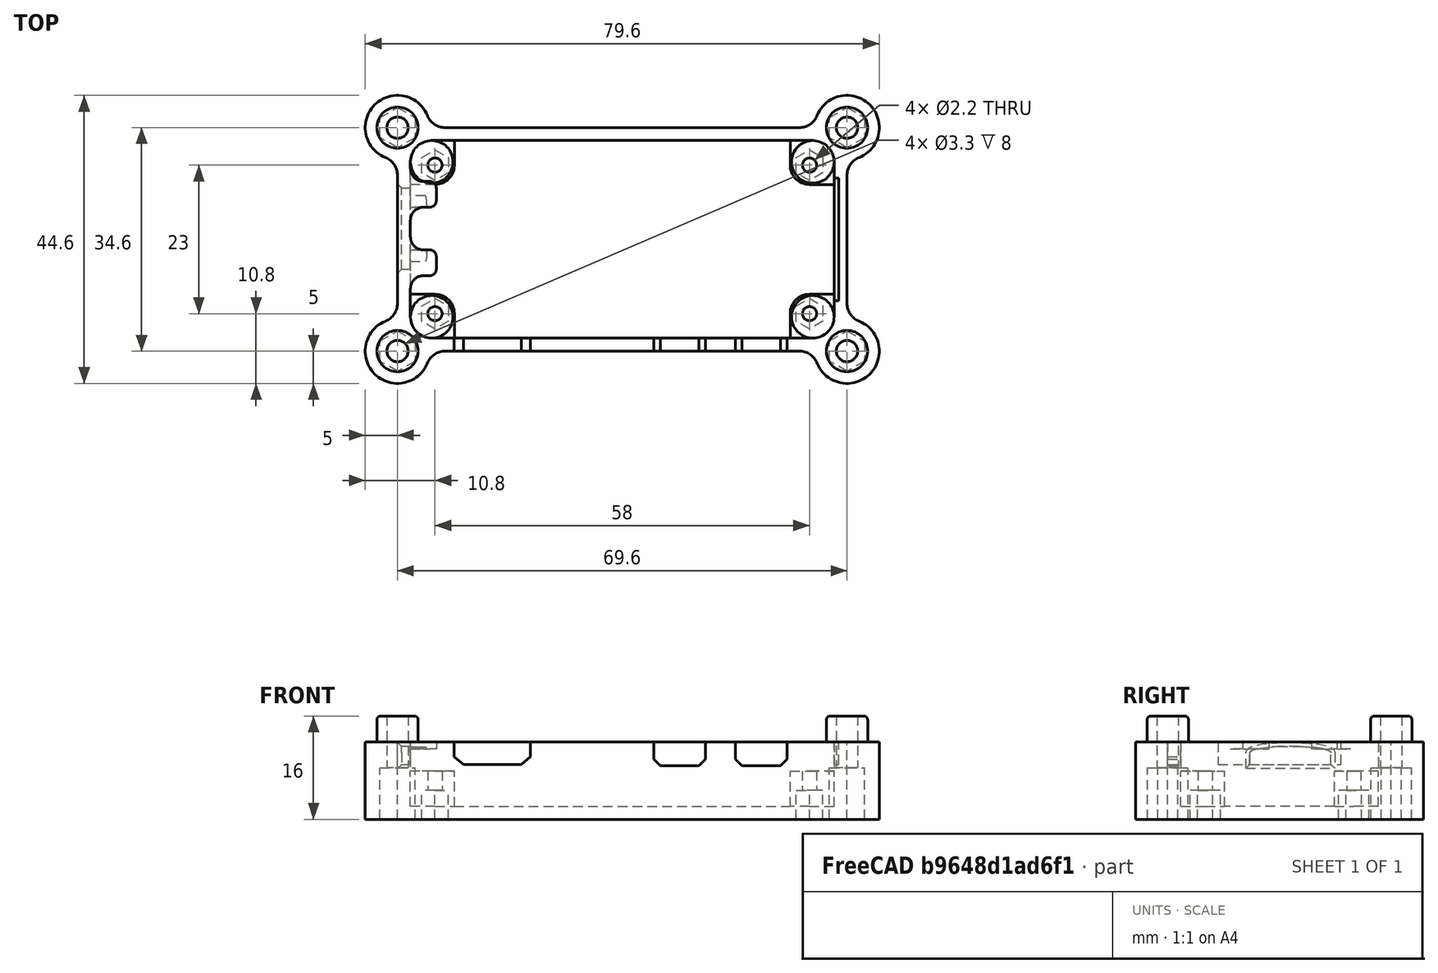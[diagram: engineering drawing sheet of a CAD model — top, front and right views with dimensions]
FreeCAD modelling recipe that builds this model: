
FCSTD DOCUMENT  (FreeCAD 0.18R13830 (Git))
Label: MMDVM_HS_Bottom
License: CreativeCommons Attribution-NonCommercial-ShareAlike
LicenseURL: http://creativecommons.org/licenses/by-nc-sa/4.0/
objects: Sketcher::SketchObject×14, PartDesign::Pocket×7, PartDesign::Fillet×5, PartDesign::Pad×4, PartDesign::Hole×2, PartDesign::Chamfer×1, PartDesign::Body×1, Mesh::Feature×1
note: 47 computed .brp shape members not serialized (recipe doc carries the construction recipe); baked Part::Feature solids carry a one-line shape summary decoded from their .brp

FEATURE [Sketcher::SketchObject] Sketch
  MapMode = 5
  Support = -> [XY_Plane]
  sketch-geometry (24):
    g0: LineSegment [constr] StartX=-32.5 StartY=15 StartZ=0 EndX=32.5 EndY=15 EndZ=0
    g1: LineSegment [constr] StartX=32.5 StartY=15 StartZ=0 EndX=32.5 EndY=-15 EndZ=0
    g2: LineSegment [constr] StartX=32.5 StartY=-15 StartZ=0 EndX=-32.5 EndY=-15 EndZ=0
    g3: LineSegment [constr] StartX=-32.5 StartY=-15 StartZ=0 EndX=-32.5 EndY=15 EndZ=0
    g4: LineSegment [constr] StartX=-29 StartY=11.5 StartZ=0 EndX=29 EndY=11.5 EndZ=0
    g5: LineSegment [constr] StartX=29 StartY=11.5 StartZ=0 EndX=29 EndY=-11.5 EndZ=0
    g6: LineSegment [constr] StartX=29 StartY=-11.5 StartZ=0 EndX=-29 EndY=-11.5 EndZ=0
    g7: LineSegment [constr] StartX=-29 StartY=-11.5 StartZ=0 EndX=-29 EndY=11.5 EndZ=0
    g8: Circle CenterX=-29 CenterY=11.5 CenterZ=0 NormalX=0 NormalY=0 NormalZ=1 AngleXU=0 Radius=1.375
    g9: Circle CenterX=29 CenterY=11.5 CenterZ=0 NormalX=0 NormalY=0 NormalZ=1 AngleXU=0 Radius=1.375
    g10: Circle CenterX=29 CenterY=-11.5 CenterZ=0 NormalX=0 NormalY=0 NormalZ=1 AngleXU=0 Radius=1.375
    g11: Circle CenterX=-29 CenterY=-11.5 CenterZ=0 NormalX=0 NormalY=0 NormalZ=1 AngleXU=0 Radius=1.375
    g12: LineSegment [constr] StartX=-29.5 StartY=12 StartZ=0 EndX=29.5 EndY=12 EndZ=0
    g13: LineSegment [constr] StartX=29.5 StartY=12 StartZ=0 EndX=29.5 EndY=-12 EndZ=0
    g14: LineSegment [constr] StartX=29.5 StartY=-12 StartZ=0 EndX=-29.5 EndY=-12 EndZ=0
    g15: LineSegment [constr] StartX=-29.5 StartY=-12 StartZ=0 EndX=-29.5 EndY=12 EndZ=0
    g16: ArcOfCircle CenterX=-29.5 CenterY=12 CenterZ=0 NormalX=0 NormalY=0 NormalZ=1 AngleXU=0 Radius=3 StartAngle=1.5708 EndAngle=3.1416
    g17: ArcOfCircle CenterX=29.5 CenterY=12 CenterZ=0 NormalX=0 NormalY=0 NormalZ=1 AngleXU=0 Radius=3 StartAngle=1.42077e-07 EndAngle=1.5708
    g18: ArcOfCircle CenterX=29.5 CenterY=-12 CenterZ=0 NormalX=0 NormalY=0 NormalZ=1 AngleXU=0 Radius=3 StartAngle=4.71239 EndAngle=6.28319
    g19: ArcOfCircle CenterX=-29.5 CenterY=-12 CenterZ=0 NormalX=0 NormalY=0 NormalZ=1 AngleXU=0 Radius=3 StartAngle=3.14159 EndAngle=4.71239
    g20: LineSegment StartX=-29.5 StartY=15 StartZ=0 EndX=29.5 EndY=15 EndZ=0
    g21: LineSegment StartX=32.5 StartY=12 StartZ=0 EndX=32.5 EndY=-12 EndZ=0
    g22: LineSegment StartX=29.5 StartY=-15 StartZ=0 EndX=-29.5 EndY=-15 EndZ=0
    g23: LineSegment StartX=-32.5 StartY=-12 StartZ=0 EndX=-32.5 EndY=12 EndZ=0
  constraints (68):
    c: Coincident(g0,g1)
    c: Coincident(g1,g2)
    c: Coincident(g2,g3)
    c: Coincident(g3,g0)
    c: Horizontal(g0)
    c: Horizontal(g2)
    c: Vertical(g1)
    c: Vertical(g3)
    c: DistanceX(g0,g0) = 65
    c: DistanceY(g1,g1) = 30
    c: Symmetric(g0,g0,g-2)
    c: Symmetric(g0,g1,g-1)
    c: Coincident(g4,g5)
    c: Coincident(g5,g6)
    c: Coincident(g6,g7)
    c: Coincident(g7,g4)
    c: Horizontal(g4)
    c: Horizontal(g6)
    c: Vertical(g5)
    c: Vertical(g7)
    c: DistanceX(g4,g4) = 58
    c: DistanceY(g5,g5) = 23
    c: Symmetric(g4,g5,g-1)
    c: Symmetric(g4,g4,g-2)
    c: Coincident(g8,g4)
    c: Coincident(g9,g4)
    c: Coincident(g10,g5)
    c: Coincident(g11,g6)
    c: Radius(g11) = 1.375
    c: Radius(g8) = 1.375
    c: Radius(g9) = 1.375
    c: Radius(g10) = 1.375
    c: Coincident(g12,g13)
    c: Coincident(g13,g14)
    c: Coincident(g14,g15)
    c: Coincident(g15,g12)
    c: Horizontal(g12)
    c: Horizontal(g14)
    c: Vertical(g13)
    c: Vertical(g15)
    c: DistanceX(g4,g12) = 0.5
    c: DistanceY(g4,g12) = 0.5
    c: DistanceY(g13,g5) = 0.5
    c: DistanceX(g14,g6) = 0.5
    c: Coincident(g16,g12)
    c: Radius(g16) = 3
    c: Coincident(g17,g12)
    c: Radius(g17) = 3
    c: Coincident(g18,g13)
    c: Radius(g18) = 3
    c: Coincident(g19,g14)
    c: Radius(g19) = 3
    c: PointOnObject(g16,g0)
    c: PointOnObject(g17,g1)
    c: PointOnObject(g18,g2)
    c: PointOnObject(g19,g3)
    c: Coincident(g20,g16)
    c: Horizontal(g20)
    c: Coincident(g20,g17)
    c: Coincident(g21,g17)
    c: Vertical(g21)
    c: Coincident(g18,g21)
    c: Coincident(g22,g18)
    c: Horizontal(g22)
    c: Coincident(g19,g22)
    c: Coincident(g23,g19)
    c: Vertical(g23)
    c: Coincident(g23,g16)
FEATURE [Sketcher::SketchObject] Sketch001
  MapMode = 5
  Support = -> [XY_Plane]
  expr: Constraints[8] = Sketch.Constraints[8]
  expr: Constraints[41] = Sketch.Constraints[41]
  expr: Constraints[9] = Sketch.Constraints[9]
  expr: Constraints[45] = Sketch.Constraints[45]
  expr: Constraints[43] = Sketch.Constraints[43]
  expr: Constraints[42] = Sketch.Constraints[42]
  expr: Constraints[20] = Sketch.Constraints[20]
  expr: Constraints[21] = Sketch.Constraints[21]
  expr: Constraints[28] = Sketch.Constraints[28]
  expr: Constraints[29] = Sketch.Constraints[29]
  expr: Constraints[30] = Sketch.Constraints[30]
  expr: Constraints[40] = Sketch.Constraints[40]
  expr: Constraints[31] = Sketch.Constraints[31]
  expr: Constraints[47] = Sketch.Constraints[47]
  expr: Constraints[49] = Sketch.Constraints[49]
  expr: Constraints[51] = Sketch.Constraints[51]
  sketch-geometry (64):
    g0: LineSegment [constr] StartX=-32.5 StartY=15 StartZ=0 EndX=32.5 EndY=15 EndZ=0
    g1: LineSegment [constr] StartX=32.5 StartY=15 StartZ=0 EndX=32.5 EndY=-15 EndZ=0
    g2: LineSegment [constr] StartX=32.5 StartY=-15 StartZ=0 EndX=-32.5 EndY=-15 EndZ=0
    g3: LineSegment [constr] StartX=-32.5 StartY=-15 StartZ=0 EndX=-32.5 EndY=15 EndZ=0
    g4: LineSegment [constr] StartX=-29 StartY=11.5 StartZ=0 EndX=29 EndY=11.5 EndZ=0
    g5: LineSegment [constr] StartX=29 StartY=11.5 StartZ=0 EndX=29 EndY=-11.5 EndZ=0
    g6: LineSegment [constr] StartX=29 StartY=-11.5 StartZ=0 EndX=-29 EndY=-11.5 EndZ=0
    g7: LineSegment [constr] StartX=-29 StartY=-11.5 StartZ=0 EndX=-29 EndY=11.5 EndZ=0
    g8: Circle [constr] CenterX=-29 CenterY=11.5 CenterZ=0 NormalX=0 NormalY=0 NormalZ=1 AngleXU=0 Radius=1.375
    g9: Circle [constr] CenterX=29 CenterY=11.5 CenterZ=0 NormalX=0 NormalY=0 NormalZ=1 AngleXU=0 Radius=1.375
    g10: Circle [constr] CenterX=29 CenterY=-11.5 CenterZ=0 NormalX=0 NormalY=0 NormalZ=1 AngleXU=0 Radius=1.375
    g11: Circle [constr] CenterX=-29 CenterY=-11.5 CenterZ=0 NormalX=0 NormalY=0 NormalZ=1 AngleXU=0 Radius=1.375
    g12: LineSegment [constr] StartX=-29.5 StartY=12 StartZ=0 EndX=29.5 EndY=12 EndZ=0
    g13: LineSegment [constr] StartX=29.5 StartY=12 StartZ=0 EndX=29.5 EndY=-12 EndZ=0
    g14: LineSegment [constr] StartX=29.5 StartY=-12 StartZ=0 EndX=-29.5 EndY=-12 EndZ=0
    g15: LineSegment [constr] StartX=-29.5 StartY=-12 StartZ=0 EndX=-29.5 EndY=12 EndZ=0
    g16: ArcOfCircle [constr] CenterX=-29.5 CenterY=12 CenterZ=0 NormalX=0 NormalY=0 NormalZ=1 AngleXU=0 Radius=3 StartAngle=1.5708 EndAngle=3.14159
    g17: ArcOfCircle [constr] CenterX=29.5 CenterY=12 CenterZ=0 NormalX=0 NormalY=0 NormalZ=1 AngleXU=0 Radius=3 StartAngle=2.8425e-08 EndAngle=1.5708
    g18: ArcOfCircle [constr] CenterX=29.5 CenterY=-12 CenterZ=0 NormalX=0 NormalY=0 NormalZ=1 AngleXU=0 Radius=3 StartAngle=4.71239 EndAngle=6.28319
    g19: ArcOfCircle [constr] CenterX=-29.5 CenterY=-12 CenterZ=0 NormalX=0 NormalY=0 NormalZ=1 AngleXU=0 Radius=3 StartAngle=3.14159 EndAngle=4.71239
    g20: LineSegment [constr] StartX=-29.5 StartY=15 StartZ=0 EndX=29.5 EndY=15 EndZ=0
    g21: LineSegment [constr] StartX=32.5 StartY=12 StartZ=0 EndX=32.5 EndY=-12 EndZ=0
    g22: LineSegment [constr] StartX=29.5 StartY=-15 StartZ=0 EndX=-29.5 EndY=-15 EndZ=0
    g23: LineSegment [constr] StartX=-32.5 StartY=-12 StartZ=0 EndX=-32.5 EndY=12 EndZ=0
    g24: ArcOfCircle [constr] CenterX=-29.5 CenterY=12 CenterZ=0 NormalX=0 NormalY=0 NormalZ=1 AngleXU=0 Radius=3.3 StartAngle=1.5708 EndAngle=3.14159
    g25: ArcOfCircle [constr] CenterX=29.5 CenterY=12 CenterZ=0 NormalX=0 NormalY=0 NormalZ=1 AngleXU=0 Radius=3.3 StartAngle=-2.2e-10 EndAngle=1.5708
    g26: ArcOfCircle [constr] CenterX=29.5 CenterY=-12 CenterZ=0 NormalX=0 NormalY=0 NormalZ=1 AngleXU=0 Radius=3.3 StartAngle=4.71239 EndAngle=6.28319
    g27: ArcOfCircle [constr] CenterX=-29.5 CenterY=-12 CenterZ=0 NormalX=0 NormalY=0 NormalZ=1 AngleXU=0 Radius=3.3 StartAngle=3.14159 EndAngle=4.71239
    g28: LineSegment [constr] StartX=-32.8 StartY=12 StartZ=0 EndX=-32.8 EndY=-12 EndZ=0
    g29: LineSegment [constr] StartX=-29.5 StartY=15.3 StartZ=0 EndX=29.5 EndY=15.3 EndZ=0
    g30: LineSegment [constr] StartX=32.8 StartY=12 StartZ=0 EndX=32.8 EndY=-12 EndZ=0
    g31: LineSegment [constr] StartX=29.5 StartY=-15.3 StartZ=0 EndX=-29.5 EndY=-15.3 EndZ=0
    g32: LineSegment [constr] StartX=-34.8 StartY=17.3 StartZ=0 EndX=34.8 EndY=17.3 EndZ=0
    g33: LineSegment [constr] StartX=34.8 StartY=17.3 StartZ=0 EndX=34.8 EndY=-17.3 EndZ=0
    g34: LineSegment [constr] StartX=34.8 StartY=-17.3 StartZ=0 EndX=-34.8 EndY=-17.3 EndZ=0
    g35: LineSegment [constr] StartX=-34.8 StartY=-17.3 StartZ=0 EndX=-34.8 EndY=17.3 EndZ=0
    g36: Circle [constr] CenterX=34.8 CenterY=17.3 CenterZ=0 NormalX=0 NormalY=0 NormalZ=1 AngleXU=0 Radius=5
    g37: Circle [constr] CenterX=34.8 CenterY=-17.3 CenterZ=0 NormalX=0 NormalY=0 NormalZ=1 AngleXU=0 Radius=5
    g38: Circle [constr] CenterX=-34.8 CenterY=-17.3 CenterZ=0 NormalX=0 NormalY=0 NormalZ=1 AngleXU=0 Radius=5
    g39: Circle [constr] CenterX=-34.8 CenterY=17.3 CenterZ=0 NormalX=0 NormalY=0 NormalZ=1 AngleXU=0 Radius=5
    g40: Circle [constr] CenterX=27.3838 CenterY=20.3 CenterZ=0 NormalX=0 NormalY=0 NormalZ=1 AngleXU=0 Radius=3
    g41: Circle [constr] CenterX=-27.3838 CenterY=20.3 CenterZ=0 NormalX=0 NormalY=0 NormalZ=1 AngleXU=0 Radius=3
    g42: Circle [constr] CenterX=-37.8 CenterY=9.8838 CenterZ=0 NormalX=0 NormalY=0 NormalZ=1 AngleXU=0 Radius=3
    g43: Circle [constr] CenterX=-37.8 CenterY=-9.8838 CenterZ=0 NormalX=0 NormalY=0 NormalZ=1 AngleXU=0 Radius=3
    g44: Circle [constr] CenterX=-27.3838 CenterY=-20.3 CenterZ=0 NormalX=0 NormalY=0 NormalZ=1 AngleXU=0 Radius=3
    g45: Circle [constr] CenterX=27.3838 CenterY=-20.3 CenterZ=0 NormalX=0 NormalY=0 NormalZ=1 AngleXU=0 Radius=3
    g46: Circle [constr] CenterX=37.8 CenterY=-9.8838 CenterZ=0 NormalX=0 NormalY=0 NormalZ=1 AngleXU=0 Radius=3
    g47: Circle [constr] CenterX=37.8 CenterY=9.8838 CenterZ=0 NormalX=0 NormalY=0 NormalZ=1 AngleXU=0 Radius=3
    g48: ArcOfCircle CenterX=34.8 CenterY=17.3 CenterZ=0 NormalX=0 NormalY=0 NormalZ=1 AngleXU=0 Radius=5 StartAngle=5.09679 EndAngle=9.04038
    g49: ArcOfCircle CenterX=27.3838 CenterY=20.3 CenterZ=0 NormalX=0 NormalY=0 NormalZ=1 AngleXU=0 Radius=3 StartAngle=4.71239 EndAngle=5.89879
    g50: ArcOfCircle CenterX=37.8 CenterY=9.8838 CenterZ=0 NormalX=0 NormalY=0 NormalZ=1 AngleXU=0 Radius=3 StartAngle=1.95519 EndAngle=3.14159
    g51: ArcOfCircle CenterX=37.8 CenterY=-9.8838 CenterZ=0 NormalX=0 NormalY=0 NormalZ=1 AngleXU=0 Radius=3 StartAngle=3.14159 EndAngle=4.32799
    g52: ArcOfCircle CenterX=34.8 CenterY=-17.3 CenterZ=0 NormalX=0 NormalY=0 NormalZ=1 AngleXU=0 Radius=5 StartAngle=3.52599 EndAngle=7.46958
    g53: ArcOfCircle CenterX=27.3838 CenterY=-20.3 CenterZ=0 NormalX=0 NormalY=0 NormalZ=1 AngleXU=0 Radius=3 StartAngle=0.384397 EndAngle=1.5708
    g54: ArcOfCircle CenterX=-27.3838 CenterY=-20.3 CenterZ=0 NormalX=0 NormalY=0 NormalZ=1 AngleXU=0 Radius=3 StartAngle=1.5708 EndAngle=2.7572
    g55: ArcOfCircle CenterX=-34.8 CenterY=-17.3 CenterZ=0 NormalX=0 NormalY=0 NormalZ=1 AngleXU=0 Radius=5 StartAngle=1.95519 EndAngle=5.89879
    g56: ArcOfCircle CenterX=-37.8 CenterY=-9.8838 CenterZ=0 NormalX=0 NormalY=0 NormalZ=1 AngleXU=0 Radius=3 StartAngle=5.09679 EndAngle=6.28319
    g57: ArcOfCircle CenterX=-37.8 CenterY=9.8838 CenterZ=0 NormalX=0 NormalY=0 NormalZ=1 AngleXU=0 Radius=3 StartAngle=6.28319 EndAngle=7.46958
    g58: ArcOfCircle CenterX=-34.8 CenterY=17.3 CenterZ=0 NormalX=0 NormalY=0 NormalZ=1 AngleXU=0 Radius=5 StartAngle=0.384397 EndAngle=4.32799
    g59: ArcOfCircle CenterX=-27.3838 CenterY=20.3 CenterZ=0 NormalX=0 NormalY=0 NormalZ=1 AngleXU=0 Radius=3 StartAngle=3.52599 EndAngle=4.71239
    g60: LineSegment StartX=-27.3838 StartY=17.3 StartZ=0 EndX=27.3838 EndY=17.3 EndZ=0
    g61: LineSegment StartX=34.8 StartY=9.8838 StartZ=0 EndX=34.8 EndY=-9.8838 EndZ=0
    g62: LineSegment StartX=27.3838 StartY=-17.3 StartZ=0 EndX=-27.3838 EndY=-17.3 EndZ=0
    g63: LineSegment StartX=-34.8 StartY=-9.8838 StartZ=0 EndX=-34.8 EndY=9.8838 EndZ=0
  constraints (184):
    c: Coincident(g0,g1)
    c: Coincident(g1,g2)
    c: Coincident(g2,g3)
    c: Coincident(g3,g0)
    c: Horizontal(g0)
    c: Horizontal(g2)
    c: Vertical(g1)
    c: Vertical(g3)
    c: DistanceX(g0,g0) = 65
    c: DistanceY(g1,g1) = 30
    c: Symmetric(g0,g0,g-2)
    c: Symmetric(g0,g1,g-1)
    c: Coincident(g4,g5)
    c: Coincident(g5,g6)
    c: Coincident(g6,g7)
    c: Coincident(g7,g4)
    c: Horizontal(g4)
    c: Horizontal(g6)
    c: Vertical(g5)
    c: Vertical(g7)
    c: DistanceX(g4,g4) = 58
    c: DistanceY(g5,g5) = 23
    c: Symmetric(g4,g5,g-1)
    c: Symmetric(g4,g4,g-2)
    c: Coincident(g8,g4)
    c: Coincident(g9,g4)
    c: Coincident(g10,g5)
    c: Coincident(g11,g6)
    c: Radius(g11) = 1.375
    c: Radius(g8) = 1.375
    c: Radius(g9) = 1.375
    c: Radius(g10) = 1.375
    c: Coincident(g12,g13)
    c: Coincident(g13,g14)
    c: Coincident(g14,g15)
    c: Coincident(g15,g12)
    c: Horizontal(g12)
    c: Horizontal(g14)
    c: Vertical(g13)
    c: Vertical(g15)
    c: DistanceX(g4,g12) = 0.5
    c: DistanceY(g4,g12) = 0.5
    c: DistanceY(g13,g5) = 0.5
    c: DistanceX(g14,g6) = 0.5
    c: Coincident(g16,g12)
    c: Radius(g16) = 3
    c: Coincident(g17,g12)
    c: Radius(g17) = 3
    c: Coincident(g18,g13)
    c: Radius(g18) = 3
    c: Coincident(g19,g14)
    c: Radius(g19) = 3
    c: PointOnObject(g16,g0)
    c: PointOnObject(g17,g1)
    c: PointOnObject(g18,g2)
    c: PointOnObject(g19,g3)
    c: Coincident(g20,g16)
    c: Horizontal(g20)
    c: Coincident(g20,g17)
    c: Coincident(g21,g17)
    c: Vertical(g21)
    c: Coincident(g18,g21)
    c: Coincident(g22,g18)
    c: Horizontal(g22)
    c: Coincident(g19,g22)
    c: Coincident(g23,g19)
    c: Vertical(g23)
    c: Coincident(g23,g16)
    c: Coincident(g24,g12)
    c: Radius(g24) = 3.3
    c: Coincident(g25,g12)
    c: Radius(g25) = 3.3
    c: Coincident(g26,g13)
    c: Radius(g26) = 3.3
    c: Coincident(g27,g14)
    c: Radius(g27) = 3.3
    c: Vertical(g28)
    c: DistanceX(g28,g2) = 0.3
    c: Coincident(g27,g28)
    c: Coincident(g28,g24)
    c: Horizontal(g29)
    c: DistanceY(g0,g29) = 0.3
    c: Coincident(g24,g29)
    c: Coincident(g25,g29)
    c: Vertical(g30)
    c: DistanceX(g0,g30) = 0.3
    c: Coincident(g25,g30)
    c: Coincident(g30,g26)
    c: Horizontal(g31)
    c: DistanceY(g31,g1) = 0.3
    c: Coincident(g31,g26)
    c: Coincident(g31,g27)
    c: Coincident(g32,g33)
    c: Coincident(g33,g34)
    c: Coincident(g34,g35)
    c: Coincident(g35,g32)
    c: Horizontal(g32)
    c: Horizontal(g34)
    c: Vertical(g33)
    c: Vertical(g35)
    c: DistanceY(g25,g32) = 2
    c: DistanceX(g25,g32) = 2
    c: DistanceY(g33,g26) = 2
    c: DistanceX(g34,g27) = 2
    c: Coincident(g36,g32)
    c: Coincident(g37,g33)
    c: Coincident(g38,g34)
    c: Coincident(g39,g32)
    c: Radius(g39) = 5
    c: Radius(g38) = 5
    c: Radius(g37) = 5
    c: Radius(g36) = 5
    c: Radius(g40) = 3
    c: Tangent(g40,g36)
    c: Tangent(g40,g32)
    c: Tangent(g47,g36)
    c: Radius(g47) = 3
    c: Tangent(g47,g33)
    c: Radius(g46) = 3
    c: Tangent(g46,g37)
    c: Tangent(g46,g33)
    c: Radius(g45) = 3
    c: Tangent(g45,g37)
    c: Tangent(g45,g34)
    c: Radius(g44) = 3
    c: Tangent(g44,g34)
    c: Tangent(g44,g38)
    c: Radius(g43) = 3
    c: Tangent(g43,g38)
    c: Tangent(g43,g35)
    c: Radius(g42) = 3
    c: Tangent(g42,g35)
    c: Tangent(g42,g39)
    c: Radius(g41) = 3
    c: Tangent(g41,g32)
    c: Tangent(g41,g39)
    c: Coincident(g48,g32)
    c: PointOnObject(g48,g36)
    c: Coincident(g49,g40)
    c: PointOnObject(g49,g40)
    c: Coincident(g50,g47)
    c: PointOnObject(g50,g47)
    c: Coincident(g51,g46)
    c: PointOnObject(g51,g46)
    c: Coincident(g52,g33)
    c: PointOnObject(g52,g37)
    c: Coincident(g53,g45)
    c: PointOnObject(g53,g45)
    c: Coincident(g54,g44)
    c: PointOnObject(g54,g44)
    c: Coincident(g55,g34)
    c: PointOnObject(g55,g38)
    c: Coincident(g56,g43)
    c: PointOnObject(g56,g43)
    c: Coincident(g57,g42)
    c: PointOnObject(g57,g42)
    c: Coincident(g58,g32)
    c: PointOnObject(g58,g39)
    c: Coincident(g59,g41)
    c: PointOnObject(g59,g41)
    c: Coincident(g49,g48)
    c: Coincident(g48,g50)
    c: Coincident(g51,g52)
    c: Coincident(g52,g53)
    c: Coincident(g54,g55)
    c: Coincident(g55,g56)
    c: Coincident(g57,g58)
    c: Coincident(g58,g59)
    c: PointOnObject(g60,g32)
    c: Horizontal(g60)
    c: PointOnObject(g61,g33)
    c: Vertical(g61)
    c: PointOnObject(g62,g34)
    c: Horizontal(g62)
    c: PointOnObject(g63,g35)
    c: Vertical(g63)
    c: Coincident(g59,g60)
    c: Coincident(g60,g49)
    c: Coincident(g50,g61)
    c: Coincident(g61,g51)
    c: Coincident(g53,g62)
    c: Coincident(g54,g62)
    c: Coincident(g56,g63)
    c: Coincident(g57,g63)
FEATURE [PartDesign::Pad] Pad
  Length = 12
  Length2 = 100
  Profile = -> Sketch001
  Type = 0
FEATURE [Sketcher::SketchObject] Sketch002
  MapMode = 5
  Placement = pos=(0,0,12) rot=(0,0,1;0rad)
  Support = -> [Pad]
  expr: Constraints[133] = Sketch001.Constraints[133]
  expr: Constraints[130] = Sketch001.Constraints[130]
  expr: Constraints[112] = Sketch001.Constraints[112]
  expr: Constraints[127] = Sketch001.Constraints[127]
  expr: Constraints[124] = Sketch001.Constraints[124]
  expr: Constraints[110] = Sketch001.Constraints[110]
  expr: Constraints[51] = Sketch001.Constraints[51]
  expr: Constraints[100] = Sketch001.Constraints[100]
  expr: Constraints[77] = Sketch001.Constraints[77]
  expr: Constraints[89] = Sketch001.Constraints[89]
  expr: Constraints[118] = Sketch001.Constraints[118]
  expr: Constraints[85] = Sketch001.Constraints[85]
  expr: Constraints[103] = Sketch001.Constraints[103]
  expr: Constraints[111] = Sketch001.Constraints[111]
  expr: Constraints[71] = Sketch001.Constraints[71]
  expr: Constraints[49] = Sketch001.Constraints[49]
  expr: Constraints[102] = Sketch001.Constraints[102]
  expr: Constraints[69] = Sketch001.Constraints[69]
  expr: Constraints[47] = Sketch001.Constraints[47]
  expr: Constraints[73] = Sketch001.Constraints[73]
  expr: Constraints[75] = Sketch001.Constraints[75]
  expr: Constraints[31] = Sketch001.Constraints[31]
  expr: Constraints[116] = Sketch001.Constraints[116]
  expr: Constraints[40] = Sketch001.Constraints[40]
  expr: Constraints[30] = Sketch001.Constraints[30]
  expr: Constraints[29] = Sketch001.Constraints[29]
  expr: Constraints[121] = Sketch001.Constraints[121]
  expr: Constraints[28] = Sketch001.Constraints[28]
  expr: Constraints[21] = Sketch001.Constraints[21]
  expr: Constraints[20] = Sketch001.Constraints[20]
  expr: Constraints[108] = Sketch001.Constraints[108]
  expr: Constraints[45] = Sketch001.Constraints[45]
  expr: Constraints[42] = Sketch001.Constraints[42]
  expr: Constraints[43] = Sketch001.Constraints[43]
  expr: Constraints[101] = Sketch001.Constraints[101]
  expr: Constraints[109] = Sketch001.Constraints[109]
  expr: Constraints[41] = Sketch001.Constraints[41]
  expr: Constraints[9] = Sketch001.Constraints[9]
  expr: Constraints[81] = Sketch001.Constraints[81]
  expr: Constraints[8] = Sketch001.Constraints[8]
  sketch-geometry (64):
    g0: LineSegment [constr] StartX=-32.5 StartY=15 StartZ=0 EndX=32.5 EndY=15 EndZ=0
    g1: LineSegment [constr] StartX=32.5 StartY=15 StartZ=0 EndX=32.5 EndY=-15 EndZ=0
    g2: LineSegment [constr] StartX=32.5 StartY=-15 StartZ=0 EndX=-32.5 EndY=-15 EndZ=0
    g3: LineSegment [constr] StartX=-32.5 StartY=-15 StartZ=0 EndX=-32.5 EndY=15 EndZ=0
    g4: LineSegment [constr] StartX=-29 StartY=11.5 StartZ=0 EndX=29 EndY=11.5 EndZ=0
    g5: LineSegment [constr] StartX=29 StartY=11.5 StartZ=0 EndX=29 EndY=-11.5 EndZ=0
    g6: LineSegment [constr] StartX=29 StartY=-11.5 StartZ=0 EndX=-29 EndY=-11.5 EndZ=0
    g7: LineSegment [constr] StartX=-29 StartY=-11.5 StartZ=0 EndX=-29 EndY=11.5 EndZ=0
    g8: Circle [constr] CenterX=-29 CenterY=11.5 CenterZ=0 NormalX=0 NormalY=0 NormalZ=1 AngleXU=0 Radius=1.375
    g9: Circle [constr] CenterX=29 CenterY=11.5 CenterZ=0 NormalX=0 NormalY=0 NormalZ=1 AngleXU=0 Radius=1.375
    g10: Circle [constr] CenterX=29 CenterY=-11.5 CenterZ=0 NormalX=0 NormalY=0 NormalZ=1 AngleXU=0 Radius=1.375
    g11: Circle [constr] CenterX=-29 CenterY=-11.5 CenterZ=0 NormalX=0 NormalY=0 NormalZ=1 AngleXU=0 Radius=1.375
    g12: LineSegment [constr] StartX=-29.5 StartY=12 StartZ=0 EndX=29.5 EndY=12 EndZ=0
    g13: LineSegment [constr] StartX=29.5 StartY=12 StartZ=0 EndX=29.5 EndY=-12 EndZ=0
    g14: LineSegment [constr] StartX=29.5 StartY=-12 StartZ=0 EndX=-29.5 EndY=-12 EndZ=0
    g15: LineSegment [constr] StartX=-29.5 StartY=-12 StartZ=0 EndX=-29.5 EndY=12 EndZ=0
    g16: ArcOfCircle [constr] CenterX=-29.5 CenterY=12 CenterZ=0 NormalX=0 NormalY=0 NormalZ=1 AngleXU=0 Radius=3 StartAngle=1.5708 EndAngle=3.14159
    g17: ArcOfCircle [constr] CenterX=29.5 CenterY=12 CenterZ=0 NormalX=0 NormalY=0 NormalZ=1 AngleXU=0 Radius=3 StartAngle=2.8425e-08 EndAngle=1.5708
    g18: ArcOfCircle [constr] CenterX=29.5 CenterY=-12 CenterZ=0 NormalX=0 NormalY=0 NormalZ=1 AngleXU=0 Radius=3 StartAngle=4.71239 EndAngle=6.28319
    g19: ArcOfCircle [constr] CenterX=-29.5 CenterY=-12 CenterZ=0 NormalX=0 NormalY=0 NormalZ=1 AngleXU=0 Radius=3 StartAngle=3.14159 EndAngle=4.71239
    g20: LineSegment [constr] StartX=-29.5 StartY=15 StartZ=0 EndX=29.5 EndY=15 EndZ=0
    g21: LineSegment [constr] StartX=32.5 StartY=12 StartZ=0 EndX=32.5 EndY=-12 EndZ=0
    g22: LineSegment [constr] StartX=29.5 StartY=-15 StartZ=0 EndX=-29.5 EndY=-15 EndZ=0
    g23: LineSegment [constr] StartX=-32.5 StartY=-12 StartZ=0 EndX=-32.5 EndY=12 EndZ=0
    g24: ArcOfCircle CenterX=-29.5 CenterY=12 CenterZ=0 NormalX=0 NormalY=0 NormalZ=1 AngleXU=0 Radius=3.3 StartAngle=1.5708 EndAngle=3.14159
    g25: ArcOfCircle CenterX=29.5 CenterY=12 CenterZ=0 NormalX=0 NormalY=0 NormalZ=1 AngleXU=0 Radius=3.3 StartAngle=-2.2e-10 EndAngle=1.5708
    g26: ArcOfCircle CenterX=29.5 CenterY=-12 CenterZ=0 NormalX=0 NormalY=0 NormalZ=1 AngleXU=0 Radius=3.3 StartAngle=4.71239 EndAngle=6.28319
    g27: ArcOfCircle CenterX=-29.5 CenterY=-12 CenterZ=0 NormalX=0 NormalY=0 NormalZ=1 AngleXU=0 Radius=3.3 StartAngle=3.14159 EndAngle=4.71239
    g28: LineSegment StartX=-32.8 StartY=12 StartZ=0 EndX=-32.8 EndY=-12 EndZ=0
    g29: LineSegment StartX=-29.5 StartY=15.3 StartZ=0 EndX=29.5 EndY=15.3 EndZ=0
    g30: LineSegment StartX=32.8 StartY=12 StartZ=0 EndX=32.8 EndY=-12 EndZ=0
    g31: LineSegment StartX=29.5 StartY=-15.3 StartZ=0 EndX=-29.5 EndY=-15.3 EndZ=0
    g32: LineSegment [constr] StartX=-34.8 StartY=17.3 StartZ=0 EndX=34.8 EndY=17.3 EndZ=0
    g33: LineSegment [constr] StartX=34.8 StartY=17.3 StartZ=0 EndX=34.8 EndY=-17.3 EndZ=0
    g34: LineSegment [constr] StartX=34.8 StartY=-17.3 StartZ=0 EndX=-34.8 EndY=-17.3 EndZ=0
    g35: LineSegment [constr] StartX=-34.8 StartY=-17.3 StartZ=0 EndX=-34.8 EndY=17.3 EndZ=0
    g36: Circle [constr] CenterX=34.8 CenterY=17.3 CenterZ=0 NormalX=0 NormalY=0 NormalZ=1 AngleXU=0 Radius=5
    g37: Circle [constr] CenterX=34.8 CenterY=-17.3 CenterZ=0 NormalX=0 NormalY=0 NormalZ=1 AngleXU=0 Radius=5
    g38: Circle [constr] CenterX=-34.8 CenterY=-17.3 CenterZ=0 NormalX=0 NormalY=0 NormalZ=1 AngleXU=0 Radius=5
    g39: Circle [constr] CenterX=-34.8 CenterY=17.3 CenterZ=0 NormalX=0 NormalY=0 NormalZ=1 AngleXU=0 Radius=5
    g40: Circle [constr] CenterX=27.3838 CenterY=20.3 CenterZ=0 NormalX=0 NormalY=0 NormalZ=1 AngleXU=0 Radius=3
    g41: Circle [constr] CenterX=-27.3838 CenterY=20.3 CenterZ=0 NormalX=0 NormalY=0 NormalZ=1 AngleXU=0 Radius=3
    g42: Circle [constr] CenterX=-37.8 CenterY=9.8838 CenterZ=0 NormalX=0 NormalY=0 NormalZ=1 AngleXU=0 Radius=3
    g43: Circle [constr] CenterX=-37.8 CenterY=-9.8838 CenterZ=0 NormalX=0 NormalY=0 NormalZ=1 AngleXU=0 Radius=3
    g44: Circle [constr] CenterX=-27.3838 CenterY=-20.3 CenterZ=0 NormalX=0 NormalY=0 NormalZ=1 AngleXU=0 Radius=3
    g45: Circle [constr] CenterX=27.3838 CenterY=-20.3 CenterZ=0 NormalX=0 NormalY=0 NormalZ=1 AngleXU=0 Radius=3
    g46: Circle [constr] CenterX=37.8 CenterY=-9.8838 CenterZ=0 NormalX=0 NormalY=0 NormalZ=1 AngleXU=0 Radius=3
    g47: Circle [constr] CenterX=37.8 CenterY=9.8838 CenterZ=0 NormalX=0 NormalY=0 NormalZ=1 AngleXU=0 Radius=3
    g48: ArcOfCircle [constr] CenterX=34.8 CenterY=17.3 CenterZ=0 NormalX=0 NormalY=0 NormalZ=1 AngleXU=0 Radius=5 StartAngle=5.09679 EndAngle=9.04038
    g49: ArcOfCircle [constr] CenterX=27.3838 CenterY=20.3 CenterZ=0 NormalX=0 NormalY=0 NormalZ=1 AngleXU=0 Radius=3 StartAngle=4.71239 EndAngle=5.89879
    g50: ArcOfCircle [constr] CenterX=37.8 CenterY=9.8838 CenterZ=0 NormalX=0 NormalY=0 NormalZ=1 AngleXU=0 Radius=3 StartAngle=1.95519 EndAngle=3.14159
    g51: ArcOfCircle [constr] CenterX=37.8 CenterY=-9.8838 CenterZ=0 NormalX=0 NormalY=0 NormalZ=1 AngleXU=0 Radius=3 StartAngle=3.14159 EndAngle=4.32799
    g52: ArcOfCircle [constr] CenterX=34.8 CenterY=-17.3 CenterZ=0 NormalX=0 NormalY=0 NormalZ=1 AngleXU=0 Radius=5 StartAngle=3.52599 EndAngle=7.46958
    g53: ArcOfCircle [constr] CenterX=27.3838 CenterY=-20.3 CenterZ=0 NormalX=0 NormalY=0 NormalZ=1 AngleXU=0 Radius=3 StartAngle=0.384397 EndAngle=1.5708
    g54: ArcOfCircle [constr] CenterX=-27.3838 CenterY=-20.3 CenterZ=0 NormalX=0 NormalY=0 NormalZ=1 AngleXU=0 Radius=3 StartAngle=1.5708 EndAngle=2.7572
    g55: ArcOfCircle [constr] CenterX=-34.8 CenterY=-17.3 CenterZ=0 NormalX=0 NormalY=0 NormalZ=1 AngleXU=0 Radius=5 StartAngle=1.95519 EndAngle=5.89879
    g56: ArcOfCircle [constr] CenterX=-37.8 CenterY=-9.8838 CenterZ=0 NormalX=0 NormalY=0 NormalZ=1 AngleXU=0 Radius=3 StartAngle=5.09679 EndAngle=6.28319
    g57: ArcOfCircle [constr] CenterX=-37.8 CenterY=9.8838 CenterZ=0 NormalX=0 NormalY=0 NormalZ=1 AngleXU=0 Radius=3 StartAngle=6.28319 EndAngle=7.46958
    g58: ArcOfCircle [constr] CenterX=-34.8 CenterY=17.3 CenterZ=0 NormalX=0 NormalY=0 NormalZ=1 AngleXU=0 Radius=5 StartAngle=0.384397 EndAngle=4.32799
    g59: ArcOfCircle [constr] CenterX=-27.3838 CenterY=20.3 CenterZ=0 NormalX=0 NormalY=0 NormalZ=1 AngleXU=0 Radius=3 StartAngle=3.52599 EndAngle=4.71239
    g60: LineSegment [constr] StartX=-27.3838 StartY=17.3 StartZ=0 EndX=27.3838 EndY=17.3 EndZ=0
    g61: LineSegment [constr] StartX=34.8 StartY=9.8838 StartZ=0 EndX=34.8 EndY=-9.8838 EndZ=0
    g62: LineSegment [constr] StartX=27.3838 StartY=-17.3 StartZ=0 EndX=-27.3838 EndY=-17.3 EndZ=0
    g63: LineSegment [constr] StartX=-34.8 StartY=-9.8838 StartZ=0 EndX=-34.8 EndY=9.8838 EndZ=0
  constraints (184):
    c: Coincident(g0,g1)
    c: Coincident(g1,g2)
    c: Coincident(g2,g3)
    c: Coincident(g3,g0)
    c: Horizontal(g0)
    c: Horizontal(g2)
    c: Vertical(g1)
    c: Vertical(g3)
    c: DistanceX(g0,g0) = 65
    c: DistanceY(g1,g1) = 30
    c: Symmetric(g0,g0,g-2)
    c: Symmetric(g0,g1,g-1)
    c: Coincident(g4,g5)
    c: Coincident(g5,g6)
    c: Coincident(g6,g7)
    c: Coincident(g7,g4)
    c: Horizontal(g4)
    c: Horizontal(g6)
    c: Vertical(g5)
    c: Vertical(g7)
    c: DistanceX(g4,g4) = 58
    c: DistanceY(g5,g5) = 23
    c: Symmetric(g4,g5,g-1)
    c: Symmetric(g4,g4,g-2)
    c: Coincident(g8,g4)
    c: Coincident(g9,g4)
    c: Coincident(g10,g5)
    c: Coincident(g11,g6)
    c: Radius(g11) = 1.375
    c: Radius(g8) = 1.375
    c: Radius(g9) = 1.375
    c: Radius(g10) = 1.375
    c: Coincident(g12,g13)
    c: Coincident(g13,g14)
    c: Coincident(g14,g15)
    c: Coincident(g15,g12)
    c: Horizontal(g12)
    c: Horizontal(g14)
    c: Vertical(g13)
    c: Vertical(g15)
    c: DistanceX(g4,g12) = 0.5
    c: DistanceY(g4,g12) = 0.5
    c: DistanceY(g13,g5) = 0.5
    c: DistanceX(g14,g6) = 0.5
    c: Coincident(g16,g12)
    c: Radius(g16) = 3
    c: Coincident(g17,g12)
    c: Radius(g17) = 3
    c: Coincident(g18,g13)
    c: Radius(g18) = 3
    c: Coincident(g19,g14)
    c: Radius(g19) = 3
    c: PointOnObject(g16,g0)
    c: PointOnObject(g17,g1)
    c: PointOnObject(g18,g2)
    c: PointOnObject(g19,g3)
    c: Coincident(g20,g16)
    c: Horizontal(g20)
    c: Coincident(g20,g17)
    c: Coincident(g21,g17)
    c: Vertical(g21)
    c: Coincident(g18,g21)
    c: Coincident(g22,g18)
    c: Horizontal(g22)
    c: Coincident(g19,g22)
    c: Coincident(g23,g19)
    c: Vertical(g23)
    c: Coincident(g23,g16)
    c: Coincident(g24,g12)
    c: Radius(g24) = 3.3
    c: Coincident(g25,g12)
    c: Radius(g25) = 3.3
    c: Coincident(g26,g13)
    c: Radius(g26) = 3.3
    c: Coincident(g27,g14)
    c: Radius(g27) = 3.3
    c: Vertical(g28)
    c: DistanceX(g28,g2) = 0.3
    c: Coincident(g27,g28)
    c: Coincident(g28,g24)
    c: Horizontal(g29)
    c: DistanceY(g0,g29) = 0.3
    c: Coincident(g24,g29)
    c: Coincident(g25,g29)
    c: Vertical(g30)
    c: DistanceX(g0,g30) = 0.3
    c: Coincident(g25,g30)
    c: Coincident(g30,g26)
    c: Horizontal(g31)
    c: DistanceY(g31,g1) = 0.3
    c: Coincident(g31,g26)
    c: Coincident(g31,g27)
    c: Coincident(g32,g33)
    c: Coincident(g33,g34)
    c: Coincident(g34,g35)
    c: Coincident(g35,g32)
    c: Horizontal(g32)
    c: Horizontal(g34)
    c: Vertical(g33)
    c: Vertical(g35)
    c: DistanceY(g25,g32) = 2
    c: DistanceX(g25,g32) = 2
    c: DistanceY(g33,g26) = 2
    c: DistanceX(g34,g27) = 2
    c: Coincident(g36,g32)
    c: Coincident(g37,g33)
    c: Coincident(g38,g34)
    c: Coincident(g39,g32)
    c: Radius(g39) = 5
    c: Radius(g38) = 5
    c: Radius(g37) = 5
    c: Radius(g36) = 5
    c: Radius(g40) = 3
    c: Tangent(g40,g36)
    c: Tangent(g40,g32)
    c: Tangent(g47,g36)
    c: Radius(g47) = 3
    c: Tangent(g47,g33)
    c: Radius(g46) = 3
    c: Tangent(g46,g37)
    c: Tangent(g46,g33)
    c: Radius(g45) = 3
    c: Tangent(g45,g37)
    c: Tangent(g45,g34)
    c: Radius(g44) = 3
    c: Tangent(g44,g34)
    c: Tangent(g44,g38)
    c: Radius(g43) = 3
    c: Tangent(g43,g38)
    c: Tangent(g43,g35)
    c: Radius(g42) = 3
    c: Tangent(g42,g35)
    c: Tangent(g42,g39)
    c: Radius(g41) = 3
    c: Tangent(g41,g32)
    c: Tangent(g41,g39)
    c: Coincident(g48,g32)
    c: PointOnObject(g48,g36)
    c: Coincident(g49,g40)
    c: PointOnObject(g49,g40)
    c: Coincident(g50,g47)
    c: PointOnObject(g50,g47)
    c: Coincident(g51,g46)
    c: PointOnObject(g51,g46)
    c: Coincident(g52,g33)
    c: PointOnObject(g52,g37)
    c: Coincident(g53,g45)
    c: PointOnObject(g53,g45)
    c: Coincident(g54,g44)
    c: PointOnObject(g54,g44)
    c: Coincident(g55,g34)
    c: PointOnObject(g55,g38)
    c: Coincident(g56,g43)
    c: PointOnObject(g56,g43)
    c: Coincident(g57,g42)
    c: PointOnObject(g57,g42)
    c: Coincident(g58,g32)
    c: PointOnObject(g58,g39)
    c: Coincident(g59,g41)
    c: PointOnObject(g59,g41)
    c: Coincident(g49,g48)
    c: Coincident(g48,g50)
    c: Coincident(g51,g52)
    c: Coincident(g52,g53)
    c: Coincident(g54,g55)
    c: Coincident(g55,g56)
    c: Coincident(g57,g58)
    c: Coincident(g58,g59)
    c: PointOnObject(g60,g32)
    c: Horizontal(g60)
    c: PointOnObject(g61,g33)
    c: Vertical(g61)
    c: PointOnObject(g62,g34)
    c: Horizontal(g62)
    c: PointOnObject(g63,g35)
    c: Vertical(g63)
    c: Coincident(g59,g60)
    c: Coincident(g60,g49)
    c: Coincident(g50,g61)
    c: Coincident(g61,g51)
    c: Coincident(g53,g62)
    c: Coincident(g54,g62)
    c: Coincident(g56,g63)
    c: Coincident(g57,g63)
FEATURE [PartDesign::Pocket] Pocket
  BaseFeature = -> Pad
  Length = 10
  Length2 = 100
  Profile = -> Sketch002
  Type = 0
FEATURE [Sketcher::SketchObject] Sketch003
  MapMode = 5
  Placement = pos=(0,0,2) rot=(0,0,1;0rad)
  Support = -> [Pocket]
  expr: Constraints[133] = Sketch002.Constraints[133]
  expr: Constraints[130] = Sketch002.Constraints[130]
  expr: Constraints[112] = Sketch002.Constraints[112]
  expr: Constraints[124] = Sketch002.Constraints[124]
  expr: Constraints[127] = Sketch002.Constraints[127]
  expr: Constraints[110] = Sketch002.Constraints[110]
  expr: Constraints[51] = Sketch002.Constraints[51]
  expr: Constraints[100] = Sketch002.Constraints[100]
  expr: Constraints[77] = Sketch002.Constraints[77]
  expr: Constraints[89] = Sketch002.Constraints[89]
  expr: Constraints[118] = Sketch002.Constraints[118]
  expr: Constraints[85] = Sketch002.Constraints[85]
  expr: Constraints[71] = Sketch002.Constraints[71]
  expr: Constraints[103] = Sketch002.Constraints[103]
  expr: Constraints[111] = Sketch002.Constraints[111]
  expr: Constraints[102] = Sketch002.Constraints[102]
  expr: Constraints[49] = Sketch002.Constraints[49]
  expr: Constraints[69] = Sketch002.Constraints[69]
  expr: Constraints[75] = Sketch002.Constraints[75]
  expr: Constraints[73] = Sketch002.Constraints[73]
  expr: Constraints[47] = Sketch002.Constraints[47]
  expr: Constraints[31] = Sketch002.Constraints[31]
  expr: Constraints[40] = Sketch002.Constraints[40]
  expr: Constraints[116] = Sketch002.Constraints[116]
  expr: Constraints[30] = Sketch002.Constraints[30]
  expr: Constraints[29] = Sketch002.Constraints[29]
  expr: Constraints[28] = Sketch002.Constraints[28]
  expr: Constraints[121] = Sketch002.Constraints[121]
  expr: Constraints[21] = Sketch002.Constraints[21]
  expr: Constraints[20] = Sketch002.Constraints[20]
  expr: Constraints[45] = Sketch002.Constraints[45]
  expr: Constraints[108] = Sketch002.Constraints[108]
  expr: Constraints[42] = Sketch002.Constraints[42]
  expr: Constraints[43] = Sketch002.Constraints[43]
  expr: Constraints[101] = Sketch002.Constraints[101]
  expr: Constraints[109] = Sketch002.Constraints[109]
  expr: Constraints[41] = Sketch002.Constraints[41]
  expr: Constraints[9] = Sketch002.Constraints[9]
  expr: Constraints[81] = Sketch002.Constraints[81]
  expr: Constraints[8] = Sketch002.Constraints[8]
  sketch-geometry (92):
    g0: LineSegment [constr] StartX=-32.5 StartY=15 StartZ=0 EndX=32.5 EndY=15 EndZ=0
    g1: LineSegment [constr] StartX=32.5 StartY=15 StartZ=0 EndX=32.5 EndY=-15 EndZ=0
    g2: LineSegment [constr] StartX=32.5 StartY=-15 StartZ=0 EndX=-32.5 EndY=-15 EndZ=0
    g3: LineSegment [constr] StartX=-32.5 StartY=-15 StartZ=0 EndX=-32.5 EndY=15 EndZ=0
    g4: LineSegment [constr] StartX=-29 StartY=11.5 StartZ=0 EndX=29 EndY=11.5 EndZ=0
    g5: LineSegment [constr] StartX=29 StartY=11.5 StartZ=0 EndX=29 EndY=-11.5 EndZ=0
    g6: LineSegment [constr] StartX=29 StartY=-11.5 StartZ=0 EndX=-29 EndY=-11.5 EndZ=0
    g7: LineSegment [constr] StartX=-29 StartY=-11.5 StartZ=0 EndX=-29 EndY=11.5 EndZ=0
    g8: Circle [constr] CenterX=-29 CenterY=11.5 CenterZ=0 NormalX=0 NormalY=0 NormalZ=1 AngleXU=0 Radius=1.375
    g9: Circle [constr] CenterX=29 CenterY=11.5 CenterZ=0 NormalX=0 NormalY=0 NormalZ=1 AngleXU=0 Radius=1.375
    g10: Circle [constr] CenterX=29 CenterY=-11.5 CenterZ=0 NormalX=0 NormalY=0 NormalZ=1 AngleXU=0 Radius=1.375
    g11: Circle [constr] CenterX=-29 CenterY=-11.5 CenterZ=0 NormalX=0 NormalY=0 NormalZ=1 AngleXU=0 Radius=1.375
    g12: LineSegment [constr] StartX=-29.5 StartY=12 StartZ=0 EndX=29.5 EndY=12 EndZ=0
    g13: LineSegment [constr] StartX=29.5 StartY=12 StartZ=0 EndX=29.5 EndY=-12 EndZ=0
    g14: LineSegment [constr] StartX=29.5 StartY=-12 StartZ=0 EndX=-29.5 EndY=-12 EndZ=0
    g15: LineSegment [constr] StartX=-29.5 StartY=-12 StartZ=0 EndX=-29.5 EndY=12 EndZ=0
    g16: ArcOfCircle [constr] CenterX=-29.5 CenterY=12 CenterZ=0 NormalX=0 NormalY=0 NormalZ=1 AngleXU=0 Radius=3 StartAngle=1.5708 EndAngle=3.14159
    g17: ArcOfCircle [constr] CenterX=29.5 CenterY=12 CenterZ=0 NormalX=0 NormalY=0 NormalZ=1 AngleXU=0 Radius=3 StartAngle=3.6972e-08 EndAngle=1.5708
    g18: ArcOfCircle [constr] CenterX=29.5 CenterY=-12 CenterZ=0 NormalX=0 NormalY=0 NormalZ=1 AngleXU=0 Radius=3 StartAngle=4.71239 EndAngle=6.28319
    g19: ArcOfCircle [constr] CenterX=-29.5 CenterY=-12 CenterZ=0 NormalX=0 NormalY=0 NormalZ=1 AngleXU=0 Radius=3 StartAngle=3.14159 EndAngle=4.71239
    g20: LineSegment [constr] StartX=-29.5 StartY=15 StartZ=0 EndX=29.5 EndY=15 EndZ=0
    g21: LineSegment [constr] StartX=32.5 StartY=12 StartZ=0 EndX=32.5 EndY=-12 EndZ=0
    g22: LineSegment [constr] StartX=29.5 StartY=-15 StartZ=0 EndX=-29.5 EndY=-15 EndZ=0
    g23: LineSegment [constr] StartX=-32.5 StartY=-12 StartZ=0 EndX=-32.5 EndY=12 EndZ=0
    g24: ArcOfCircle [constr] CenterX=-29.5 CenterY=12 CenterZ=0 NormalX=0 NormalY=0 NormalZ=1 AngleXU=0 Radius=3.3 StartAngle=1.5708 EndAngle=3.14159
    g25: ArcOfCircle [constr] CenterX=29.5 CenterY=12 CenterZ=0 NormalX=0 NormalY=0 NormalZ=1 AngleXU=0 Radius=3.3 StartAngle=-4.27e-10 EndAngle=1.5708
    g26: ArcOfCircle [constr] CenterX=29.5 CenterY=-12 CenterZ=0 NormalX=0 NormalY=0 NormalZ=1 AngleXU=0 Radius=3.3 StartAngle=4.71239 EndAngle=6.28319
    g27: ArcOfCircle [constr] CenterX=-29.5 CenterY=-12 CenterZ=0 NormalX=0 NormalY=0 NormalZ=1 AngleXU=0 Radius=3.3 StartAngle=3.14159 EndAngle=4.71239
    g28: LineSegment [constr] StartX=-32.8 StartY=12 StartZ=0 EndX=-32.8 EndY=-12 EndZ=0
    g29: LineSegment [constr] StartX=-29.5 StartY=15.3 StartZ=0 EndX=29.5 EndY=15.3 EndZ=0
    g30: LineSegment [constr] StartX=32.8 StartY=12 StartZ=0 EndX=32.8 EndY=-12 EndZ=0
    g31: LineSegment [constr] StartX=29.5 StartY=-15.3 StartZ=0 EndX=-29.5 EndY=-15.3 EndZ=0
    g32: LineSegment [constr] StartX=-34.8 StartY=17.3 StartZ=0 EndX=34.8 EndY=17.3 EndZ=0
    g33: LineSegment [constr] StartX=34.8 StartY=17.3 StartZ=0 EndX=34.8 EndY=-17.3 EndZ=0
    g34: LineSegment [constr] StartX=34.8 StartY=-17.3 StartZ=0 EndX=-34.8 EndY=-17.3 EndZ=0
    g35: LineSegment [constr] StartX=-34.8 StartY=-17.3 StartZ=0 EndX=-34.8 EndY=17.3 EndZ=0
    g36: Circle [constr] CenterX=34.8 CenterY=17.3 CenterZ=0 NormalX=0 NormalY=0 NormalZ=1 AngleXU=0 Radius=5
    g37: Circle [constr] CenterX=34.8 CenterY=-17.3 CenterZ=0 NormalX=0 NormalY=0 NormalZ=1 AngleXU=0 Radius=5
    g38: Circle [constr] CenterX=-34.8 CenterY=-17.3 CenterZ=0 NormalX=0 NormalY=0 NormalZ=1 AngleXU=0 Radius=5
    g39: Circle [constr] CenterX=-34.8 CenterY=17.3 CenterZ=0 NormalX=0 NormalY=0 NormalZ=1 AngleXU=0 Radius=5
    g40: Circle [constr] CenterX=27.3838 CenterY=20.3 CenterZ=0 NormalX=0 NormalY=0 NormalZ=1 AngleXU=0 Radius=3
    g41: Circle [constr] CenterX=-27.3838 CenterY=20.3 CenterZ=0 NormalX=0 NormalY=0 NormalZ=1 AngleXU=0 Radius=3
    g42: Circle [constr] CenterX=-37.8 CenterY=9.8838 CenterZ=0 NormalX=0 NormalY=0 NormalZ=1 AngleXU=0 Radius=3
    g43: Circle [constr] CenterX=-37.8 CenterY=-9.8838 CenterZ=0 NormalX=0 NormalY=0 NormalZ=1 AngleXU=0 Radius=3
    g44: Circle [constr] CenterX=-27.3838 CenterY=-20.3 CenterZ=0 NormalX=0 NormalY=0 NormalZ=1 AngleXU=0 Radius=3
    g45: Circle [constr] CenterX=27.3838 CenterY=-20.3 CenterZ=0 NormalX=0 NormalY=0 NormalZ=1 AngleXU=0 Radius=3
    g46: Circle [constr] CenterX=37.8 CenterY=-9.8838 CenterZ=0 NormalX=0 NormalY=0 NormalZ=1 AngleXU=0 Radius=3
    g47: Circle [constr] CenterX=37.8 CenterY=9.8838 CenterZ=0 NormalX=0 NormalY=0 NormalZ=1 AngleXU=0 Radius=3
    g48: ArcOfCircle [constr] CenterX=34.8 CenterY=17.3 CenterZ=0 NormalX=0 NormalY=0 NormalZ=1 AngleXU=0 Radius=5 StartAngle=5.09679 EndAngle=9.04038
    g49: ArcOfCircle [constr] CenterX=27.3838 CenterY=20.3 CenterZ=0 NormalX=0 NormalY=0 NormalZ=1 AngleXU=0 Radius=3 StartAngle=4.71239 EndAngle=5.89879
    g50: ArcOfCircle [constr] CenterX=37.8 CenterY=9.8838 CenterZ=0 NormalX=0 NormalY=0 NormalZ=1 AngleXU=0 Radius=3 StartAngle=1.95519 EndAngle=3.14159
    g51: ArcOfCircle [constr] CenterX=37.8 CenterY=-9.8838 CenterZ=0 NormalX=0 NormalY=0 NormalZ=1 AngleXU=0 Radius=3 StartAngle=3.14159 EndAngle=4.32799
    g52: ArcOfCircle [constr] CenterX=34.8 CenterY=-17.3 CenterZ=0 NormalX=0 NormalY=0 NormalZ=1 AngleXU=0 Radius=5 StartAngle=3.52599 EndAngle=7.46958
    g53: ArcOfCircle [constr] CenterX=27.3838 CenterY=-20.3 CenterZ=0 NormalX=0 NormalY=0 NormalZ=1 AngleXU=0 Radius=3 StartAngle=0.384397 EndAngle=1.5708
    g54: ArcOfCircle [constr] CenterX=-27.3838 CenterY=-20.3 CenterZ=0 NormalX=0 NormalY=0 NormalZ=1 AngleXU=0 Radius=3 StartAngle=1.5708 EndAngle=2.7572
    g55: ArcOfCircle [constr] CenterX=-34.8 CenterY=-17.3 CenterZ=0 NormalX=0 NormalY=0 NormalZ=1 AngleXU=0 Radius=5 StartAngle=1.95519 EndAngle=5.89879
    g56: ArcOfCircle [constr] CenterX=-37.8 CenterY=-9.8838 CenterZ=0 NormalX=0 NormalY=0 NormalZ=1 AngleXU=0 Radius=3 StartAngle=5.09678 EndAngle=6.28319
    g57: ArcOfCircle [constr] CenterX=-37.8 CenterY=9.8838 CenterZ=0 NormalX=0 NormalY=0 NormalZ=1 AngleXU=0 Radius=3 StartAngle=4.4909e-08 EndAngle=1.1864
    g58: ArcOfCircle [constr] CenterX=-34.8 CenterY=17.3 CenterZ=0 NormalX=0 NormalY=0 NormalZ=1 AngleXU=0 Radius=5 StartAngle=0.384397 EndAngle=4.32799
    g59: ArcOfCircle [constr] CenterX=-27.3838 CenterY=20.3 CenterZ=0 NormalX=0 NormalY=0 NormalZ=1 AngleXU=0 Radius=3 StartAngle=3.52599 EndAngle=4.71239
    g60: LineSegment [constr] StartX=-27.3838 StartY=17.3 StartZ=0 EndX=27.3838 EndY=17.3 EndZ=0
    g61: LineSegment [constr] StartX=34.8 StartY=9.8838 StartZ=0 EndX=34.8 EndY=-9.8838 EndZ=0
    g62: LineSegment [constr] StartX=27.3838 StartY=-17.3 StartZ=0 EndX=-27.3838 EndY=-17.3 EndZ=0
    g63: LineSegment [constr] StartX=-34.8 StartY=-9.8838 StartZ=0 EndX=-34.8 EndY=9.8838 EndZ=0
    g64: ArcOfCircle CenterX=29 CenterY=11.5 CenterZ=0 NormalX=0 NormalY=0 NormalZ=1 AngleXU=0 Radius=3 StartAngle=3.14352 EndAngle=4.71046
    g65: ArcOfCircle CenterX=29.5 CenterY=12 CenterZ=0 NormalX=0 NormalY=0 NormalZ=1 AngleXU=0 Radius=3.3 StartAngle=2.17631e-07 EndAngle=1.5708
    g66: LineSegment StartX=26 StartY=15.3 StartZ=0 EndX=29.5 EndY=15.3 EndZ=0
    g67: LineSegment StartX=32.8 StartY=12 StartZ=0 EndX=32.8 EndY=8.50001 EndZ=0
    g68: LineSegment StartX=26 StartY=15.3 StartZ=0 EndX=26 EndY=11.4942 EndZ=0
    g69: LineSegment StartX=28.9942 StartY=8.50001 StartZ=0 EndX=32.8 EndY=8.50001 EndZ=0
    g70: LineSegment [constr] StartX=-43.6068 StartY=0 StartZ=0 EndX=51.9839 EndY=0 EndZ=0
    g71: LineSegment [constr] StartX=0 StartY=-19.8111 StartZ=0 EndX=0 EndY=22.459 EndZ=0
    g72: LineSegment StartX=26 StartY=-15.3 StartZ=0 EndX=26 EndY=-11.4942 EndZ=0
    g73: ArcOfCircle CenterX=29 CenterY=-11.5 CenterZ=0 NormalX=0 NormalY=0 NormalZ=1 AngleXU=0 Radius=3 StartAngle=1.57273 EndAngle=3.13966
    g74: LineSegment StartX=28.9942 StartY=-8.50001 StartZ=0 EndX=32.8 EndY=-8.50001 EndZ=0
    g75: LineSegment StartX=26 StartY=-15.3 StartZ=0 EndX=29.5 EndY=-15.3 EndZ=0
    g76: ArcOfCircle CenterX=29.5 CenterY=-12 CenterZ=0 NormalX=0 NormalY=0 NormalZ=1 AngleXU=0 Radius=3.3 StartAngle=4.71238 EndAngle=6.28319
    g77: LineSegment StartX=32.8 StartY=-12 StartZ=0 EndX=32.8 EndY=-8.50001 EndZ=0
    g78: LineSegment StartX=-28.9942 StartY=-8.50001 StartZ=0 EndX=-32.8 EndY=-8.50001 EndZ=0
    g79: LineSegment StartX=-32.8 StartY=-12 StartZ=0 EndX=-32.8 EndY=-8.50001 EndZ=0
    g80: ArcOfCircle CenterX=-29.5 CenterY=-12 CenterZ=0 NormalX=0 NormalY=0 NormalZ=1 AngleXU=0 Radius=3.3 StartAngle=3.14159 EndAngle=4.71239
    g81: LineSegment StartX=-26 StartY=-15.3 StartZ=0 EndX=-29.5 EndY=-15.3 EndZ=0
    g82: LineSegment StartX=-26 StartY=-15.3 StartZ=0 EndX=-26 EndY=-11.4942 EndZ=0
    g83: ArcOfCircle CenterX=-29 CenterY=-11.5 CenterZ=0 NormalX=0 NormalY=0 NormalZ=1 AngleXU=0 Radius=3 StartAngle=0.00192871 EndAngle=1.56886
    g84: LineSegment StartX=-28.9942 StartY=8.50001 StartZ=0 EndX=-32.8 EndY=8.50001 EndZ=0
    g85: LineSegment StartX=-32.8 StartY=12 StartZ=0 EndX=-32.8 EndY=8.50001 EndZ=0
    g86: ArcOfCircle CenterX=-29.5 CenterY=12 CenterZ=0 NormalX=0 NormalY=0 NormalZ=1 AngleXU=0 Radius=3.3 StartAngle=1.57079 EndAngle=3.14159
    g87: LineSegment StartX=-26 StartY=15.3 StartZ=0 EndX=-29.5 EndY=15.3 EndZ=0
    g88: LineSegment StartX=-26 StartY=15.3 StartZ=0 EndX=-26 EndY=11.4942 EndZ=0
    g89: ArcOfCircle CenterX=-29 CenterY=11.5 CenterZ=0 NormalX=0 NormalY=0 NormalZ=1 AngleXU=0 Radius=3 StartAngle=4.71432 EndAngle=6.28126
    g90: Circle CenterX=29 CenterY=11.5 CenterZ=0 NormalX=0 NormalY=0 NormalZ=1 AngleXU=0 Radius=0.5
    g91: Circle CenterX=-29 CenterY=-11.5 CenterZ=0 NormalX=0 NormalY=0 NormalZ=1 AngleXU=0 Radius=0.5
  constraints (241):
    c: Coincident(g0,g1)
    c: Coincident(g1,g2)
    c: Coincident(g2,g3)
    c: Coincident(g3,g0)
    c: Horizontal(g0)
    c: Horizontal(g2)
    c: Vertical(g1)
    c: Vertical(g3)
    c: DistanceX(g0,g0) = 65
    c: DistanceY(g1,g1) = 30
    c: Symmetric(g0,g0,g-2)
    c: Symmetric(g0,g1,g-1)
    c: Coincident(g4,g5)
    c: Coincident(g5,g6)
    c: Coincident(g6,g7)
    c: Coincident(g7,g4)
    c: Horizontal(g4)
    c: Horizontal(g6)
    c: Vertical(g5)
    c: Vertical(g7)
    c: DistanceX(g4,g4) = 58
    c: DistanceY(g5,g5) = 23
    c: Symmetric(g4,g5,g-1)
    c: Symmetric(g4,g4,g-2)
    c: Coincident(g8,g4)
    c: Coincident(g9,g4)
    c: Coincident(g10,g5)
    c: Coincident(g11,g6)
    c: Radius(g11) = 1.375
    c: Radius(g8) = 1.375
    c: Radius(g9) = 1.375
    c: Radius(g10) = 1.375
    c: Coincident(g12,g13)
    c: Coincident(g13,g14)
    c: Coincident(g14,g15)
    c: Coincident(g15,g12)
    c: Horizontal(g12)
    c: Horizontal(g14)
    c: Vertical(g13)
    c: Vertical(g15)
    c: DistanceX(g4,g12) = 0.5
    c: DistanceY(g4,g12) = 0.5
    c: DistanceY(g13,g5) = 0.5
    c: DistanceX(g14,g6) = 0.5
    c: Coincident(g16,g12)
    c: Radius(g16) = 3
    c: Coincident(g17,g12)
    c: Radius(g17) = 3
    c: Coincident(g18,g13)
    c: Radius(g18) = 3
    c: Coincident(g19,g14)
    c: Radius(g19) = 3
    c: PointOnObject(g16,g0)
    c: PointOnObject(g17,g1)
    c: PointOnObject(g18,g2)
    c: PointOnObject(g19,g3)
    c: Coincident(g20,g16)
    c: Horizontal(g20)
    c: Coincident(g20,g17)
    c: Coincident(g21,g17)
    c: Vertical(g21)
    c: Coincident(g18,g21)
    c: Coincident(g22,g18)
    c: Horizontal(g22)
    c: Coincident(g19,g22)
    c: Coincident(g23,g19)
    c: Vertical(g23)
    c: Coincident(g23,g16)
    c: Coincident(g24,g12)
    c: Radius(g24) = 3.3
    c: Coincident(g25,g12)
    c: Radius(g25) = 3.3
    c: Coincident(g26,g13)
    c: Radius(g26) = 3.3
    c: Coincident(g27,g14)
    c: Radius(g27) = 3.3
    c: Vertical(g28)
    c: DistanceX(g28,g2) = 0.3
    c: Coincident(g27,g28)
    c: Coincident(g28,g24)
    c: Horizontal(g29)
    c: DistanceY(g0,g29) = 0.3
    c: Coincident(g24,g29)
    c: Coincident(g25,g29)
    c: Vertical(g30)
    c: DistanceX(g0,g30) = 0.3
    c: Coincident(g25,g30)
    c: Coincident(g30,g26)
    c: Horizontal(g31)
    c: DistanceY(g31,g1) = 0.3
    c: Coincident(g31,g26)
    c: Coincident(g31,g27)
    c: Coincident(g32,g33)
    c: Coincident(g33,g34)
    c: Coincident(g34,g35)
    c: Coincident(g35,g32)
    c: Horizontal(g32)
    c: Horizontal(g34)
    c: Vertical(g33)
    c: Vertical(g35)
    c: DistanceY(g25,g32) = 2
    c: DistanceX(g25,g32) = 2
    c: DistanceY(g33,g26) = 2
    c: DistanceX(g34,g27) = 2
    c: Coincident(g36,g32)
    c: Coincident(g37,g33)
    c: Coincident(g38,g34)
    c: Coincident(g39,g32)
    c: Radius(g39) = 5
    c: Radius(g38) = 5
    c: Radius(g37) = 5
    c: Radius(g36) = 5
    c: Radius(g40) = 3
    c: Tangent(g40,g36)
    c: Tangent(g40,g32)
    c: Tangent(g47,g36)
    c: Radius(g47) = 3
    c: Tangent(g47,g33)
    c: Radius(g46) = 3
    c: Tangent(g46,g37)
    c: Tangent(g46,g33)
    c: Radius(g45) = 3
    c: Tangent(g45,g37)
    c: Tangent(g45,g34)
    c: Radius(g44) = 3
    c: Tangent(g44,g34)
    c: Tangent(g44,g38)
    c: Radius(g43) = 3
    c: Tangent(g43,g38)
    c: Tangent(g43,g35)
    c: Radius(g42) = 3
    c: Tangent(g42,g35)
    c: Tangent(g42,g39)
    c: Radius(g41) = 3
    c: Tangent(g41,g32)
    c: Tangent(g41,g39)
    c: Coincident(g48,g32)
    c: PointOnObject(g48,g36)
    c: Coincident(g49,g40)
    c: PointOnObject(g49,g40)
    c: Coincident(g50,g47)
    c: PointOnObject(g50,g47)
    c: Coincident(g51,g46)
    c: PointOnObject(g51,g46)
    c: Coincident(g52,g33)
    c: PointOnObject(g52,g37)
    c: Coincident(g53,g45)
    c: PointOnObject(g53,g45)
    c: Coincident(g54,g44)
    c: PointOnObject(g54,g44)
    c: Coincident(g55,g34)
    c: PointOnObject(g55,g38)
    c: Coincident(g56,g43)
    c: PointOnObject(g56,g43)
    c: Coincident(g57,g42)
    c: PointOnObject(g57,g42)
    c: Coincident(g58,g32)
    c: PointOnObject(g58,g39)
    c: Coincident(g59,g41)
    c: PointOnObject(g59,g41)
    c: Coincident(g49,g48)
    c: Coincident(g48,g50)
    c: Coincident(g51,g52)
    c: Coincident(g52,g53)
    c: Coincident(g54,g55)
    c: Coincident(g55,g56)
    c: Coincident(g57,g58)
    c: Coincident(g58,g59)
    c: PointOnObject(g60,g32)
    c: Horizontal(g60)
    c: PointOnObject(g61,g33)
    c: Vertical(g61)
    c: PointOnObject(g62,g34)
    c: Horizontal(g62)
    c: PointOnObject(g63,g35)
    c: Vertical(g63)
    c: Coincident(g59,g60)
    c: Coincident(g60,g49)
    c: Coincident(g50,g61)
    c: Coincident(g61,g51)
    c: Coincident(g53,g62)
    c: Coincident(g54,g62)
    c: Coincident(g56,g63)
    c: Coincident(g57,g63)
    c: Coincident(g64,g4)
    c: Radius(g64) = 3
    c: Coincident(g65,g12)
    c: PointOnObject(g66,g29)
    c: Horizontal(g66)
    c: Coincident(g65,g66)
    c: PointOnObject(g65,g25)
    c: PointOnObject(g67,g30)
    c: Vertical(g67)
    c: Coincident(g67,g65)
    c: Vertical(g68)
    c: Coincident(g68,g64)
    c: Coincident(g68,g66)
    c: Horizontal(g69)
    c: Coincident(g64,g69)
    c: Coincident(g67,g69)
    c: PointOnObject(g70,g-1)
    c: Horizontal(g70)
    c: PointOnObject(g71,g-2)
    c: Vertical(g71)
    c: Radius(g73) = 3
    c: Horizontal(g75)
    c: Coincident(g76,g75)
    c: Vertical(g77)
    c: Coincident(g77,g76)
    c: Vertical(g72)
    c: Coincident(g72,g73)
    c: Coincident(g72,g75)
    c: Horizontal(g74)
    c: Coincident(g73,g74)
    c: Coincident(g77,g74)
    c: Radius(g89) = 3
    c: Horizontal(g87)
    c: Coincident(g86,g87)
    c: Vertical(g85)
    c: Coincident(g85,g86)
    c: Vertical(g88)
    c: Coincident(g88,g89)
    c: Coincident(g88,g87)
    c: Horizontal(g84)
    c: Coincident(g89,g84)
    c: Coincident(g85,g84)
    c: Radius(g83) = 3
    c: Horizontal(g81)
    c: Coincident(g80,g81)
    c: Vertical(g79)
    c: Coincident(g79,g80)
    c: Vertical(g82)
    c: Coincident(g82,g83)
    c: Coincident(g82,g81)
    c: Horizontal(g78)
    c: Coincident(g83,g78)
    c: Coincident(g79,g78)
    c: Coincident(g90,g4)
    c: Radius(g90) = 0.5
    c: Coincident(g91,g6)
    c: Radius(g91) = 0.5
FEATURE [PartDesign::Pad] Pad001
  BaseFeature = -> Pocket
  Length = 5.5
  Length2 = 100
  Profile = -> Sketch003
  Type = 0
FEATURE [Sketcher::SketchObject] Sketch004
  MapMode = 5
  Placement = pos=(0,0,12) rot=(0,0,1;0rad)
  Support = -> [Pad001]
  expr: Constraints[133] = Sketch001.Constraints[133]
  expr: Constraints[130] = Sketch001.Constraints[130]
  expr: Constraints[112] = Sketch001.Constraints[112]
  expr: Constraints[124] = Sketch001.Constraints[124]
  expr: Constraints[127] = Sketch001.Constraints[127]
  expr: Constraints[110] = Sketch001.Constraints[110]
  expr: Constraints[51] = Sketch001.Constraints[51]
  expr: Constraints[100] = Sketch001.Constraints[100]
  expr: Constraints[77] = Sketch001.Constraints[77]
  expr: Constraints[89] = Sketch001.Constraints[89]
  expr: Constraints[85] = Sketch001.Constraints[85]
  expr: Constraints[118] = Sketch001.Constraints[118]
  expr: Constraints[71] = Sketch001.Constraints[71]
  expr: Constraints[111] = Sketch001.Constraints[111]
  expr: Constraints[103] = Sketch001.Constraints[103]
  expr: Constraints[49] = Sketch001.Constraints[49]
  expr: Constraints[102] = Sketch001.Constraints[102]
  expr: Constraints[69] = Sketch001.Constraints[69]
  expr: Constraints[47] = Sketch001.Constraints[47]
  expr: Constraints[73] = Sketch001.Constraints[73]
  expr: Constraints[75] = Sketch001.Constraints[75]
  expr: Constraints[31] = Sketch001.Constraints[31]
  expr: Constraints[116] = Sketch001.Constraints[116]
  expr: Constraints[40] = Sketch001.Constraints[40]
  expr: Constraints[30] = Sketch001.Constraints[30]
  expr: Constraints[29] = Sketch001.Constraints[29]
  expr: Constraints[28] = Sketch001.Constraints[28]
  expr: Constraints[121] = Sketch001.Constraints[121]
  expr: Constraints[21] = Sketch001.Constraints[21]
  expr: Constraints[20] = Sketch001.Constraints[20]
  expr: Constraints[43] = Sketch001.Constraints[43]
  expr: Constraints[42] = Sketch001.Constraints[42]
  expr: Constraints[101] = Sketch001.Constraints[101]
  expr: Constraints[108] = Sketch001.Constraints[108]
  expr: Constraints[45] = Sketch001.Constraints[45]
  expr: Constraints[41] = Sketch001.Constraints[41]
  expr: Constraints[9] = Sketch001.Constraints[9]
  expr: Constraints[81] = Sketch001.Constraints[81]
  expr: Constraints[109] = Sketch001.Constraints[109]
  expr: Constraints[8] = Sketch001.Constraints[8]
  sketch-geometry (68):
    g0: LineSegment [constr] StartX=-32.5 StartY=15 StartZ=0 EndX=32.5 EndY=15 EndZ=0
    g1: LineSegment [constr] StartX=32.5 StartY=15 StartZ=0 EndX=32.5 EndY=-15 EndZ=0
    g2: LineSegment [constr] StartX=32.5 StartY=-15 StartZ=0 EndX=-32.5 EndY=-15 EndZ=0
    g3: LineSegment [constr] StartX=-32.5 StartY=-15 StartZ=0 EndX=-32.5 EndY=15 EndZ=0
    g4: LineSegment [constr] StartX=-29 StartY=11.5 StartZ=0 EndX=29 EndY=11.5 EndZ=0
    g5: LineSegment [constr] StartX=29 StartY=11.5 StartZ=0 EndX=29 EndY=-11.5 EndZ=0
    g6: LineSegment [constr] StartX=29 StartY=-11.5 StartZ=0 EndX=-29 EndY=-11.5 EndZ=0
    g7: LineSegment [constr] StartX=-29 StartY=-11.5 StartZ=0 EndX=-29 EndY=11.5 EndZ=0
    g8: Circle [constr] CenterX=-29 CenterY=11.5 CenterZ=0 NormalX=0 NormalY=0 NormalZ=1 AngleXU=0 Radius=1.375
    g9: Circle [constr] CenterX=29 CenterY=11.5 CenterZ=0 NormalX=0 NormalY=0 NormalZ=1 AngleXU=0 Radius=1.375
    g10: Circle [constr] CenterX=29 CenterY=-11.5 CenterZ=0 NormalX=0 NormalY=0 NormalZ=1 AngleXU=0 Radius=1.375
    g11: Circle [constr] CenterX=-29 CenterY=-11.5 CenterZ=0 NormalX=0 NormalY=0 NormalZ=1 AngleXU=0 Radius=1.375
    g12: LineSegment [constr] StartX=-29.5 StartY=12 StartZ=0 EndX=29.5 EndY=12 EndZ=0
    g13: LineSegment [constr] StartX=29.5 StartY=12 StartZ=0 EndX=29.5 EndY=-12 EndZ=0
    g14: LineSegment [constr] StartX=29.5 StartY=-12 StartZ=0 EndX=-29.5 EndY=-12 EndZ=0
    g15: LineSegment [constr] StartX=-29.5 StartY=-12 StartZ=0 EndX=-29.5 EndY=12 EndZ=0
    g16: ArcOfCircle [constr] CenterX=-29.5 CenterY=12 CenterZ=0 NormalX=0 NormalY=0 NormalZ=1 AngleXU=0 Radius=3 StartAngle=1.5708 EndAngle=3.14159
    g17: ArcOfCircle [constr] CenterX=29.5 CenterY=12 CenterZ=0 NormalX=0 NormalY=0 NormalZ=1 AngleXU=0 Radius=3 StartAngle=2.8425e-08 EndAngle=1.5708
    g18: ArcOfCircle [constr] CenterX=29.5 CenterY=-12 CenterZ=0 NormalX=0 NormalY=0 NormalZ=1 AngleXU=0 Radius=3 StartAngle=4.71239 EndAngle=6.28319
    g19: ArcOfCircle [constr] CenterX=-29.5 CenterY=-12 CenterZ=0 NormalX=0 NormalY=0 NormalZ=1 AngleXU=0 Radius=3 StartAngle=3.14159 EndAngle=4.71239
    g20: LineSegment [constr] StartX=-29.5 StartY=15 StartZ=0 EndX=29.5 EndY=15 EndZ=0
    g21: LineSegment [constr] StartX=32.5 StartY=12 StartZ=0 EndX=32.5 EndY=-12 EndZ=0
    g22: LineSegment [constr] StartX=29.5 StartY=-15 StartZ=0 EndX=-29.5 EndY=-15 EndZ=0
    g23: LineSegment [constr] StartX=-32.5 StartY=-12 StartZ=0 EndX=-32.5 EndY=12 EndZ=0
    g24: ArcOfCircle [constr] CenterX=-29.5 CenterY=12 CenterZ=0 NormalX=0 NormalY=0 NormalZ=1 AngleXU=0 Radius=3.3 StartAngle=1.5708 EndAngle=3.14159
    g25: ArcOfCircle [constr] CenterX=29.5 CenterY=12 CenterZ=0 NormalX=0 NormalY=0 NormalZ=1 AngleXU=0 Radius=3.3 StartAngle=-2.2e-10 EndAngle=1.5708
    g26: ArcOfCircle [constr] CenterX=29.5 CenterY=-12 CenterZ=0 NormalX=0 NormalY=0 NormalZ=1 AngleXU=0 Radius=3.3 StartAngle=4.71239 EndAngle=6.28319
    g27: ArcOfCircle [constr] CenterX=-29.5 CenterY=-12 CenterZ=0 NormalX=0 NormalY=0 NormalZ=1 AngleXU=0 Radius=3.3 StartAngle=3.14159 EndAngle=4.71239
    g28: LineSegment [constr] StartX=-32.8 StartY=12 StartZ=0 EndX=-32.8 EndY=-12 EndZ=0
    g29: LineSegment [constr] StartX=-29.5 StartY=15.3 StartZ=0 EndX=29.5 EndY=15.3 EndZ=0
    g30: LineSegment [constr] StartX=32.8 StartY=12 StartZ=0 EndX=32.8 EndY=-12 EndZ=0
    g31: LineSegment [constr] StartX=29.5 StartY=-15.3 StartZ=0 EndX=-29.5 EndY=-15.3 EndZ=0
    g32: LineSegment [constr] StartX=-34.8 StartY=17.3 StartZ=0 EndX=34.8 EndY=17.3 EndZ=0
    g33: LineSegment [constr] StartX=34.8 StartY=17.3 StartZ=0 EndX=34.8 EndY=-17.3 EndZ=0
    g34: LineSegment [constr] StartX=34.8 StartY=-17.3 StartZ=0 EndX=-34.8 EndY=-17.3 EndZ=0
    g35: LineSegment [constr] StartX=-34.8 StartY=-17.3 StartZ=0 EndX=-34.8 EndY=17.3 EndZ=0
    g36: Circle [constr] CenterX=34.8 CenterY=17.3 CenterZ=0 NormalX=0 NormalY=0 NormalZ=1 AngleXU=0 Radius=5
    g37: Circle [constr] CenterX=34.8 CenterY=-17.3 CenterZ=0 NormalX=0 NormalY=0 NormalZ=1 AngleXU=0 Radius=5
    g38: Circle [constr] CenterX=-34.8 CenterY=-17.3 CenterZ=0 NormalX=0 NormalY=0 NormalZ=1 AngleXU=0 Radius=5
    g39: Circle [constr] CenterX=-34.8 CenterY=17.3 CenterZ=0 NormalX=0 NormalY=0 NormalZ=1 AngleXU=0 Radius=5
    g40: Circle [constr] CenterX=27.3838 CenterY=20.3 CenterZ=0 NormalX=0 NormalY=0 NormalZ=1 AngleXU=0 Radius=3
    g41: Circle [constr] CenterX=-27.3838 CenterY=20.3 CenterZ=0 NormalX=0 NormalY=0 NormalZ=1 AngleXU=0 Radius=3
    g42: Circle [constr] CenterX=-37.8 CenterY=9.8838 CenterZ=0 NormalX=0 NormalY=0 NormalZ=1 AngleXU=0 Radius=3
    g43: Circle [constr] CenterX=-37.8 CenterY=-9.8838 CenterZ=0 NormalX=0 NormalY=0 NormalZ=1 AngleXU=0 Radius=3
    g44: Circle [constr] CenterX=-27.3838 CenterY=-20.3 CenterZ=0 NormalX=0 NormalY=0 NormalZ=1 AngleXU=0 Radius=3
    g45: Circle [constr] CenterX=27.3838 CenterY=-20.3 CenterZ=0 NormalX=0 NormalY=0 NormalZ=1 AngleXU=0 Radius=3
    g46: Circle [constr] CenterX=37.8 CenterY=-9.8838 CenterZ=0 NormalX=0 NormalY=0 NormalZ=1 AngleXU=0 Radius=3
    g47: Circle [constr] CenterX=37.8 CenterY=9.8838 CenterZ=0 NormalX=0 NormalY=0 NormalZ=1 AngleXU=0 Radius=3
    g48: ArcOfCircle [constr] CenterX=34.8 CenterY=17.3 CenterZ=0 NormalX=0 NormalY=0 NormalZ=1 AngleXU=0 Radius=5 StartAngle=5.09679 EndAngle=9.04038
    g49: ArcOfCircle [constr] CenterX=27.3838 CenterY=20.3 CenterZ=0 NormalX=0 NormalY=0 NormalZ=1 AngleXU=0 Radius=3 StartAngle=4.71239 EndAngle=5.89879
    g50: ArcOfCircle [constr] CenterX=37.8 CenterY=9.8838 CenterZ=0 NormalX=0 NormalY=0 NormalZ=1 AngleXU=0 Radius=3 StartAngle=1.95519 EndAngle=3.14159
    g51: ArcOfCircle [constr] CenterX=37.8 CenterY=-9.8838 CenterZ=0 NormalX=0 NormalY=0 NormalZ=1 AngleXU=0 Radius=3 StartAngle=3.14159 EndAngle=4.32799
    g52: ArcOfCircle [constr] CenterX=34.8 CenterY=-17.3 CenterZ=0 NormalX=0 NormalY=0 NormalZ=1 AngleXU=0 Radius=5 StartAngle=3.52599 EndAngle=7.46958
    g53: ArcOfCircle [constr] CenterX=27.3838 CenterY=-20.3 CenterZ=0 NormalX=0 NormalY=0 NormalZ=1 AngleXU=0 Radius=3 StartAngle=0.384397 EndAngle=1.5708
    g54: ArcOfCircle [constr] CenterX=-27.3838 CenterY=-20.3 CenterZ=0 NormalX=0 NormalY=0 NormalZ=1 AngleXU=0 Radius=3 StartAngle=1.5708 EndAngle=2.7572
    g55: ArcOfCircle [constr] CenterX=-34.8 CenterY=-17.3 CenterZ=0 NormalX=0 NormalY=0 NormalZ=1 AngleXU=0 Radius=5 StartAngle=1.95519 EndAngle=5.89879
    g56: ArcOfCircle [constr] CenterX=-37.8 CenterY=-9.8838 CenterZ=0 NormalX=0 NormalY=0 NormalZ=1 AngleXU=0 Radius=3 StartAngle=5.09679 EndAngle=6.28319
    g57: ArcOfCircle [constr] CenterX=-37.8 CenterY=9.8838 CenterZ=0 NormalX=0 NormalY=0 NormalZ=1 AngleXU=0 Radius=3 StartAngle=6.28319 EndAngle=7.46958
    g58: ArcOfCircle [constr] CenterX=-34.8 CenterY=17.3 CenterZ=0 NormalX=0 NormalY=0 NormalZ=1 AngleXU=0 Radius=5 StartAngle=0.384397 EndAngle=4.32799
    g59: ArcOfCircle [constr] CenterX=-27.3838 CenterY=20.3 CenterZ=0 NormalX=0 NormalY=0 NormalZ=1 AngleXU=0 Radius=3 StartAngle=3.52599 EndAngle=4.71239
    g60: LineSegment [constr] StartX=-27.3838 StartY=17.3 StartZ=0 EndX=27.3838 EndY=17.3 EndZ=0
    g61: LineSegment [constr] StartX=34.8 StartY=9.8838 StartZ=0 EndX=34.8 EndY=-9.8838 EndZ=0
    g62: LineSegment [constr] StartX=27.3838 StartY=-17.3 StartZ=0 EndX=-27.3838 EndY=-17.3 EndZ=0
    g63: LineSegment [constr] StartX=-34.8 StartY=-9.8838 StartZ=0 EndX=-34.8 EndY=9.8838 EndZ=0
    g64: Circle CenterX=34.8 CenterY=17.3 CenterZ=0 NormalX=0 NormalY=0 NormalZ=1 AngleXU=0 Radius=3.2
    g65: Circle CenterX=34.8 CenterY=-17.3 CenterZ=0 NormalX=0 NormalY=0 NormalZ=1 AngleXU=0 Radius=3.2
    g66: Circle CenterX=-34.8 CenterY=-17.3 CenterZ=0 NormalX=0 NormalY=0 NormalZ=1 AngleXU=0 Radius=3.2
    g67: Circle CenterX=-34.8 CenterY=17.3 CenterZ=0 NormalX=0 NormalY=0 NormalZ=1 AngleXU=0 Radius=3.2
  constraints (192):
    c: Coincident(g0,g1)
    c: Coincident(g1,g2)
    c: Coincident(g2,g3)
    c: Coincident(g3,g0)
    c: Horizontal(g0)
    c: Horizontal(g2)
    c: Vertical(g1)
    c: Vertical(g3)
    c: DistanceX(g0,g0) = 65
    c: DistanceY(g1,g1) = 30
    c: Symmetric(g0,g0,g-2)
    c: Symmetric(g0,g1,g-1)
    c: Coincident(g4,g5)
    c: Coincident(g5,g6)
    c: Coincident(g6,g7)
    c: Coincident(g7,g4)
    c: Horizontal(g4)
    c: Horizontal(g6)
    c: Vertical(g5)
    c: Vertical(g7)
    c: DistanceX(g4,g4) = 58
    c: DistanceY(g5,g5) = 23
    c: Symmetric(g4,g5,g-1)
    c: Symmetric(g4,g4,g-2)
    c: Coincident(g8,g4)
    c: Coincident(g9,g4)
    c: Coincident(g10,g5)
    c: Coincident(g11,g6)
    c: Radius(g11) = 1.375
    c: Radius(g8) = 1.375
    c: Radius(g9) = 1.375
    c: Radius(g10) = 1.375
    c: Coincident(g12,g13)
    c: Coincident(g13,g14)
    c: Coincident(g14,g15)
    c: Coincident(g15,g12)
    c: Horizontal(g12)
    c: Horizontal(g14)
    c: Vertical(g13)
    c: Vertical(g15)
    c: DistanceX(g4,g12) = 0.5
    c: DistanceY(g4,g12) = 0.5
    c: DistanceY(g13,g5) = 0.5
    c: DistanceX(g14,g6) = 0.5
    c: Coincident(g16,g12)
    c: Radius(g16) = 3
    c: Coincident(g17,g12)
    c: Radius(g17) = 3
    c: Coincident(g18,g13)
    c: Radius(g18) = 3
    c: Coincident(g19,g14)
    c: Radius(g19) = 3
    c: PointOnObject(g16,g0)
    c: PointOnObject(g17,g1)
    c: PointOnObject(g18,g2)
    c: PointOnObject(g19,g3)
    c: Coincident(g20,g16)
    c: Horizontal(g20)
    c: Coincident(g20,g17)
    c: Coincident(g21,g17)
    c: Vertical(g21)
    c: Coincident(g18,g21)
    c: Coincident(g22,g18)
    c: Horizontal(g22)
    c: Coincident(g19,g22)
    c: Coincident(g23,g19)
    c: Vertical(g23)
    c: Coincident(g23,g16)
    c: Coincident(g24,g12)
    c: Radius(g24) = 3.3
    c: Coincident(g25,g12)
    c: Radius(g25) = 3.3
    c: Coincident(g26,g13)
    c: Radius(g26) = 3.3
    c: Coincident(g27,g14)
    c: Radius(g27) = 3.3
    c: Vertical(g28)
    c: DistanceX(g28,g2) = 0.3
    c: Coincident(g27,g28)
    c: Coincident(g28,g24)
    c: Horizontal(g29)
    c: DistanceY(g0,g29) = 0.3
    c: Coincident(g24,g29)
    c: Coincident(g25,g29)
    c: Vertical(g30)
    c: DistanceX(g0,g30) = 0.3
    c: Coincident(g25,g30)
    c: Coincident(g30,g26)
    c: Horizontal(g31)
    c: DistanceY(g31,g1) = 0.3
    c: Coincident(g31,g26)
    c: Coincident(g31,g27)
    c: Coincident(g32,g33)
    c: Coincident(g33,g34)
    c: Coincident(g34,g35)
    c: Coincident(g35,g32)
    c: Horizontal(g32)
    c: Horizontal(g34)
    c: Vertical(g33)
    c: Vertical(g35)
    c: DistanceY(g25,g32) = 2
    c: DistanceX(g25,g32) = 2
    c: DistanceY(g33,g26) = 2
    c: DistanceX(g34,g27) = 2
    c: Coincident(g36,g32)
    c: Coincident(g37,g33)
    c: Coincident(g38,g34)
    c: Coincident(g39,g32)
    c: Radius(g39) = 5
    c: Radius(g38) = 5
    c: Radius(g37) = 5
    c: Radius(g36) = 5
    c: Radius(g40) = 3
    c: Tangent(g40,g36)
    c: Tangent(g40,g32)
    c: Tangent(g47,g36)
    c: Radius(g47) = 3
    c: Tangent(g47,g33)
    c: Radius(g46) = 3
    c: Tangent(g46,g37)
    c: Tangent(g46,g33)
    c: Radius(g45) = 3
    c: Tangent(g45,g37)
    c: Tangent(g45,g34)
    c: Radius(g44) = 3
    c: Tangent(g44,g34)
    c: Tangent(g44,g38)
    c: Radius(g43) = 3
    c: Tangent(g43,g38)
    c: Tangent(g43,g35)
    c: Radius(g42) = 3
    c: Tangent(g42,g35)
    c: Tangent(g42,g39)
    c: Radius(g41) = 3
    c: Tangent(g41,g32)
    c: Tangent(g41,g39)
    c: Coincident(g48,g32)
    c: PointOnObject(g48,g36)
    c: Coincident(g49,g40)
    c: PointOnObject(g49,g40)
    c: Coincident(g50,g47)
    c: PointOnObject(g50,g47)
    c: Coincident(g51,g46)
    c: PointOnObject(g51,g46)
    c: Coincident(g52,g33)
    c: PointOnObject(g52,g37)
    c: Coincident(g53,g45)
    c: PointOnObject(g53,g45)
    c: Coincident(g54,g44)
    c: PointOnObject(g54,g44)
    c: Coincident(g55,g34)
    c: PointOnObject(g55,g38)
    c: Coincident(g56,g43)
    c: PointOnObject(g56,g43)
    c: Coincident(g57,g42)
    c: PointOnObject(g57,g42)
    c: Coincident(g58,g32)
    c: PointOnObject(g58,g39)
    c: Coincident(g59,g41)
    c: PointOnObject(g59,g41)
    c: Coincident(g49,g48)
    c: Coincident(g48,g50)
    c: Coincident(g51,g52)
    c: Coincident(g52,g53)
    c: Coincident(g54,g55)
    c: Coincident(g55,g56)
    c: Coincident(g57,g58)
    c: Coincident(g58,g59)
    c: PointOnObject(g60,g32)
    c: Horizontal(g60)
    c: PointOnObject(g61,g33)
    c: Vertical(g61)
    c: PointOnObject(g62,g34)
    c: Horizontal(g62)
    c: PointOnObject(g63,g35)
    c: Vertical(g63)
    c: Coincident(g59,g60)
    c: Coincident(g60,g49)
    c: Coincident(g50,g61)
    c: Coincident(g61,g51)
    c: Coincident(g53,g62)
    c: Coincident(g54,g62)
    c: Coincident(g56,g63)
    c: Coincident(g57,g63)
    c: Coincident(g64,g32)
    c: Coincident(g65,g33)
    c: Coincident(g66,g34)
    c: Coincident(g67,g32)
    c: Radius(g67) = 3.2
    c: Radius(g64) = 3.2
    c: Radius(g65) = 3.2
    c: Radius(g66) = 3.2
FEATURE [PartDesign::Pad] Pad002
  BaseFeature = -> Pad001
  Length = 4
  Length2 = 100
  Profile = -> Sketch004
  Type = 0
FEATURE [Sketcher::SketchObject] Sketch005
  MapMode = 5
  Placement = pos=(0,-17.3,0) rot=(1,0,0;1.5708rad)
  sketch-geometry (22):
    g0: LineSegment StartX=-26.0242 StartY=12 StartZ=0 EndX=-14.2242 EndY=12 EndZ=0
    g1: LineSegment StartX=-14.2242 StartY=12 StartZ=0 EndX=-14.2242 EndY=9.7 EndZ=0
    g2: LineSegment StartX=-26.0242 StartY=9.7 StartZ=0 EndX=-26.0242 EndY=12 EndZ=0
    g3: LineSegment [constr] StartX=-20.1242 StartY=16.7174 StartZ=0 EndX=-20.1242 EndY=2.05389 EndZ=0
    g4: LineSegment [constr] StartX=-26 StartY=7.5 StartZ=0 EndX=23.454 EndY=7.5 EndZ=0
    g5: LineSegment StartX=-24.5941 StartY=8.5 StartZ=0 EndX=-15.6543 EndY=8.5 EndZ=0
    g6: LineSegment StartX=-26.0242 StartY=9.7 StartZ=0 EndX=-24.5941 EndY=8.5 EndZ=0
    g7: LineSegment StartX=-15.6543 StartY=8.5 StartZ=0 EndX=-14.2242 EndY=9.7 EndZ=0
    g8: LineSegment StartX=4.8858 StartY=12 StartZ=0 EndX=12.8858 EndY=12 EndZ=0
    g9: LineSegment StartX=12.8858 StartY=12 StartZ=0 EndX=12.8858 EndY=9.28 EndZ=0
    g10: LineSegment StartX=4.8858 StartY=9.28 StartZ=0 EndX=4.8858 EndY=12 EndZ=0
    g11: LineSegment [constr] StartX=8.8858 StartY=17.7004 StartZ=0 EndX=8.8858 EndY=3.91586 EndZ=0
    g12: LineSegment StartX=4.8858 StartY=9.28 StartZ=0 EndX=5.8858 EndY=8.28 EndZ=0
    g13: LineSegment StartX=11.8858 StartY=8.28 StartZ=0 EndX=12.8858 EndY=9.28 EndZ=0
    g14: LineSegment StartX=5.8858 StartY=8.28 StartZ=0 EndX=11.8858 EndY=8.28 EndZ=0
    g15: LineSegment StartX=17.5058 StartY=12 StartZ=0 EndX=25.5058 EndY=12 EndZ=0
    g16: LineSegment StartX=25.5058 StartY=12 StartZ=0 EndX=25.5058 EndY=9.28 EndZ=0
    g17: LineSegment StartX=17.5058 StartY=9.28 StartZ=0 EndX=17.5058 EndY=12 EndZ=0
    g18: LineSegment StartX=17.5058 StartY=9.28 StartZ=0 EndX=18.5058 EndY=8.28 EndZ=0
    g19: LineSegment StartX=24.5058 StartY=8.28 StartZ=0 EndX=25.5058 EndY=9.28 EndZ=0
    g20: LineSegment StartX=18.5058 StartY=8.28 StartZ=0 EndX=24.5058 EndY=8.28 EndZ=0
    g21: LineSegment [constr] StartX=21.5058 StartY=16.2884 StartZ=0 EndX=21.5058 EndY=2.78996 EndZ=0
  constraints (57):
    c: Coincident(g0,g1)
    c: Coincident(g2,g0)
    c: Horizontal(g0)
    c: Vertical(g1)
    c: Vertical(g2)
    c: Vertical(g3)
    c: Symmetric(g0,g0,g3)
    c: DistanceX(g0,g0) = 11.8
    c: Horizontal(g4)
    c: Horizontal(g5)
    c: Angle(g5,g6) = 2.44346
    c: Angle(g7,g5) = 2.44346
    c: Coincident(g2,g6)
    c: Coincident(g6,g5)
    c: DistanceY(g5,g2) = 1.2
    c: Coincident(g7,g5)
    c: DistanceY(g5,g7) = 1.2
    c: Coincident(g1,g7)
    c: DistanceY(g4,g5) = 1
    c: Coincident(g8,g9)
    c: Coincident(g10,g8)
    c: Horizontal(g8)
    c: Vertical(g9)
    c: Vertical(g10)
    c: DistanceX(g8,g8) = 8
    c: Vertical(g11)
    c: DistanceX(g3,g11) = 29.01
    c: Symmetric(g8,g8,g11)
    c: Horizontal(g14)
    c: DistanceY(g4,g14) = 0.78
    c: Angle(g13,g14) = 2.35619
    c: Angle(g14,g12) = 2.35619
    c: Coincident(g12,g14)
    c: Coincident(g12,g10)
    c: DistanceY(g12,g10) = 1
    c: Coincident(g14,g13)
    c: Coincident(g13,g9)
    c: DistanceY(g13,g9) = 1
    c: Coincident(g15,g16)
    c: Coincident(g17,g15)
    c: Horizontal(g15)
    c: Vertical(g16)
    c: Vertical(g17)
    c: Equal(g8,g15) = 7.8
    c: Horizontal(g20)
    c: Angle(g19,g20) = 2.35619
    c: Angle(g20,g18) = 2.35619
    c: Coincident(g18,g20)
    c: Coincident(g18,g17)
    c: DistanceY(g18,g17) = 1
    c: Coincident(g20,g19)
    c: Coincident(g19,g16)
    c: DistanceY(g19,g16) = 1
    c: DistanceY(g4,g18) = 0.78
    c: Vertical(g21)
    c: DistanceX(g11,g21) = 12.62
    c: Symmetric(g15,g15,g21)
FEATURE [PartDesign::Pocket] Pocket002
  BaseFeature = -> Pad002
  Length = 5
  Length2 = 100
  Profile = -> Sketch005
  Type = 2
FEATURE [Sketcher::SketchObject] Sketch006
  ExternalGeometry = -> [Pocket002]
  MapMode = 5
  Placement = pos=(-34.8,0,0) rot=(0.57735,-0.57735,-0.57735;2.0944rad)
  Support = -> [Pocket002]
  sketch-geometry (12):
    g0: LineSegment [constr] StartX=-8.50001 StartY=7.5 StartZ=0 EndX=0.928937 EndY=7.5 EndZ=0
    g1: LineSegment [constr] StartX=-1.67421 StartY=13.4438 StartZ=0 EndX=-1.67421 EndY=3.80207 EndZ=0
    g2: LineSegment [constr] StartX=-11.4942 StartY=7.5 StartZ=0 EndX=-11.4942 EndY=14.033 EndZ=0
    g3: LineSegment StartX=4.62579 StartY=10.3 StartZ=0 EndX=4.62579 EndY=8.5 EndZ=0
    g4: LineSegment StartX=4.62579 StartY=8.5 StartZ=0 EndX=-7.97421 EndY=8.5 EndZ=0
    g5: LineSegment StartX=-7.97421 StartY=8.5 StartZ=0 EndX=-7.97421 EndY=10.3 EndZ=0
    g6: LineSegment [constr] StartX=4.62579 StartY=10.3 StartZ=0 EndX=-7.97421 EndY=10.3 EndZ=0
    g7: ArcOfEllipse CenterX=-1.67421 CenterY=10.3 CenterZ=0 NormalX=0 NormalY=0 NormalZ=1 MajorRadius=6.3 MinorRadius=1.00676 AngleXU=-3.14159 StartAngle=3.14159 EndAngle=6.28319
    g8: LineSegment [constr] StartX=-7.97421 StartY=10.3 StartZ=0 EndX=4.62579 EndY=10.3 EndZ=0
    g9: LineSegment [constr] StartX=-1.67421 StartY=9.29324 StartZ=0 EndX=-1.67421 EndY=11.3068 EndZ=0
    g10: GeomPoint X=-7.89325 Y=10.3 Z=0
    g11: GeomPoint X=4.54482 Y=10.3 Z=0
FEATURE [PartDesign::Pocket] Pocket003
  BaseFeature = -> Pocket002
  Length = 5
  Length2 = 100
  Profile = -> Sketch006
  Type = 2
FEATURE [PartDesign::Chamfer] Chamfer
  Base = -> Pocket003 [Edge60,Edge62]
  BaseFeature = -> Pocket003
  Size = 0.6
FEATURE [Sketcher::SketchObject] Sketch007
  ExternalGeometry = -> [Chamfer]
  MapMode = 5
  Placement = pos=(0,0,16) rot=(0,0,1;0rad)
  Support = -> [Chamfer]
  sketch-geometry (4):
    g0: Circle CenterX=34.8 CenterY=17.3 CenterZ=0 NormalX=0 NormalY=0 NormalZ=1 AngleXU=0 Radius=2.43827
    g1: Circle CenterX=-34.8 CenterY=17.3 CenterZ=0 NormalX=0 NormalY=0 NormalZ=1 AngleXU=0 Radius=2.44385
    g2: Circle CenterX=-34.8 CenterY=-17.3 CenterZ=0 NormalX=0 NormalY=0 NormalZ=1 AngleXU=0 Radius=2.67402
    g3: Circle CenterX=34.8 CenterY=-17.3 CenterZ=0 NormalX=0 NormalY=0 NormalZ=1 AngleXU=0 Radius=2.67742
  constraints (4):
    c: Coincident(g0,g-3)
    c: Coincident(g1,g-4)
    c: Coincident(g2,g-6)
    c: Coincident(g3,g-5)
FEATURE [PartDesign::Hole] Hole
  BaseFeature = -> Chamfer
  Depth = 25
  DepthType = 1
  Diameter = 3.3
  DrillPoint = 1
  DrillPointAngle = 118
  HoleCutCountersinkAngle = 90
  HoleCutDepth = 0
  HoleCutDiameter = 3
  HoleCutType = 0
  ModelActualThread = false
  Profile = -> Sketch007
  Tapered = false
  TaperedAngle = 90
  ThreadAngle = 0
  ThreadClass = 0
  ThreadCutOffInner = 0
  ThreadCutOffOuter = 0
  ThreadDirection = 0
  ThreadFit = 0
  ThreadPitch = 0
  ThreadSize = 3
  ThreadType = 1
  Threaded = false
FEATURE [Sketcher::SketchObject] Sketch008
  ExternalGeometry = -> [Hole]
  MapMode = 5
  Placement = pos=(0,0,0) rot=(1,0,0;3.14159rad)
  Support = -> [Hole]
  sketch-geometry (32):
    g0: LineSegment [constr] StartX=-34.8 StartY=27.181 StartZ=0 EndX=-34.8 EndY=-26.8986 EndZ=0
    g1: LineSegment [constr] StartX=34.8 StartY=-24.6336 StartZ=0 EndX=34.8 EndY=23.8401 EndZ=0
    g2: LineSegment [constr] StartX=-45.3318 StartY=17.3 StartZ=0 EndX=42.1188 EndY=17.3 EndZ=0
    g3: LineSegment [constr] StartX=-44.7382 StartY=-17.3 StartZ=0 EndX=39.4916 EndY=-17.3 EndZ=0
    g4: LineSegment StartX=34.8 StartY=14.1708 StartZ=0 EndX=37.51 EndY=15.7354 EndZ=0
    g5: LineSegment StartX=37.51 StartY=15.7354 StartZ=0 EndX=37.51 EndY=18.8646 EndZ=0
    g6: LineSegment StartX=37.51 StartY=18.8646 StartZ=0 EndX=34.8 EndY=20.4292 EndZ=0
    g7: LineSegment StartX=34.8 StartY=20.4292 StartZ=0 EndX=32.09 EndY=18.8646 EndZ=0
    g8: LineSegment StartX=32.09 StartY=18.8646 StartZ=0 EndX=32.09 EndY=15.7354 EndZ=0
    g9: LineSegment StartX=32.09 StartY=15.7354 StartZ=0 EndX=34.8 EndY=14.1708 EndZ=0
    g10: Circle [constr] CenterX=34.8 CenterY=17.3 CenterZ=0 NormalX=0 NormalY=0 NormalZ=1 AngleXU=0 Radius=3.12924
    g11: LineSegment StartX=-34.8 StartY=14.1708 StartZ=0 EndX=-32.09 EndY=15.7354 EndZ=0
    g12: LineSegment StartX=-32.09 StartY=15.7354 StartZ=0 EndX=-32.09 EndY=18.8646 EndZ=0
    g13: LineSegment StartX=-32.09 StartY=18.8646 StartZ=0 EndX=-34.8 EndY=20.4292 EndZ=0
    g14: LineSegment StartX=-34.8 StartY=20.4292 StartZ=0 EndX=-37.51 EndY=18.8646 EndZ=0
    g15: LineSegment StartX=-37.51 StartY=18.8646 StartZ=0 EndX=-37.51 EndY=15.7354 EndZ=0
    g16: LineSegment StartX=-37.51 StartY=15.7354 StartZ=0 EndX=-34.8 EndY=14.1708 EndZ=0
    g17: Circle [constr] CenterX=-34.8 CenterY=17.3 CenterZ=0 NormalX=0 NormalY=0 NormalZ=1 AngleXU=0 Radius=3.12924
    g18: LineSegment StartX=34.8 StartY=-20.4292 StartZ=0 EndX=37.51 EndY=-18.8646 EndZ=0
    g19: LineSegment StartX=37.51 StartY=-18.8646 StartZ=0 EndX=37.51 EndY=-15.7354 EndZ=0
    g20: LineSegment StartX=37.51 StartY=-15.7354 StartZ=0 EndX=34.8 EndY=-14.1708 EndZ=0
    g21: LineSegment StartX=34.8 StartY=-14.1708 StartZ=0 EndX=32.09 EndY=-15.7354 EndZ=0
    g22: LineSegment StartX=32.09 StartY=-15.7354 StartZ=0 EndX=32.09 EndY=-18.8646 EndZ=0
    g23: LineSegment StartX=32.09 StartY=-18.8646 StartZ=0 EndX=34.8 EndY=-20.4292 EndZ=0
    g24: Circle [constr] CenterX=34.8 CenterY=-17.3 CenterZ=0 NormalX=0 NormalY=0 NormalZ=1 AngleXU=0 Radius=3.12924
    g25: LineSegment StartX=-34.8 StartY=-20.4292 StartZ=0 EndX=-32.09 EndY=-18.8646 EndZ=0
    g26: LineSegment StartX=-32.09 StartY=-18.8646 StartZ=0 EndX=-32.09 EndY=-15.7354 EndZ=0
    g27: LineSegment StartX=-32.09 StartY=-15.7354 StartZ=0 EndX=-34.8 EndY=-14.1708 EndZ=0
    g28: LineSegment StartX=-34.8 StartY=-14.1708 StartZ=0 EndX=-37.51 EndY=-15.7354 EndZ=0
    g29: LineSegment StartX=-37.51 StartY=-15.7354 StartZ=0 EndX=-37.51 EndY=-18.8646 EndZ=0
    g30: LineSegment StartX=-37.51 StartY=-18.8646 StartZ=0 EndX=-34.8 EndY=-20.4292 EndZ=0
    g31: Circle [constr] CenterX=-34.8 CenterY=-17.3 CenterZ=0 NormalX=0 NormalY=0 NormalZ=1 AngleXU=0 Radius=3.12924
  constraints (72):
    c: Vertical(g0)
    c: Vertical(g1)
    c: Horizontal(g2)
    c: Horizontal(g3)
    c: PointOnObject(g-6,g3)
    c: PointOnObject(g-6,g1)
    c: PointOnObject(g-5,g0)
    c: PointOnObject(g-4,g2)
    c: Coincident(g4,g5)
    c: Coincident(g5,g6)
    c: Coincident(g6,g7)
    c: Coincident(g7,g8)
    c: Coincident(g8,g9)
    c: Coincident(g9,g4)
    c: Equal(g4, g5-g9) x5
    c: PointOnObject(g4,g10)
    c: PointOnObject(g5,g10)
    c: PointOnObject(g6,g10)
    c: PointOnObject(g7,g10)
    c: PointOnObject(g8,g10)
    c: PointOnObject(g9,g10)
    c: Coincident(g10,g-3)
    c: PointOnObject(g9,g1)
    c: DistanceX(g7,g5) = 5.42
    c: Coincident(g11,g12)
    c: Coincident(g12,g13)
    c: Coincident(g13,g14)
    c: Coincident(g14,g15)
    c: Coincident(g15,g16)
    c: Coincident(g16,g11)
    c: Equal(g11, g12-g16) x5
    c: PointOnObject(g11,g17)
    c: PointOnObject(g12,g17)
    c: PointOnObject(g13,g17)
    c: PointOnObject(g14,g17)
    c: PointOnObject(g15,g17)
    c: PointOnObject(g16,g17)
    c: Coincident(g17,g-4)
    c: PointOnObject(g16,g0)
    c: DistanceX(g14,g12) = 5.42
    c: Coincident(g18,g19)
    c: Coincident(g19,g20)
    c: Coincident(g20,g21)
    c: Coincident(g21,g22)
    c: Coincident(g22,g23)
    c: Coincident(g23,g18)
    c: Equal(g18, g19-g23) x5
    c: PointOnObject(g18,g24)
    c: PointOnObject(g19,g24)
    c: PointOnObject(g20,g24)
    c: PointOnObject(g21,g24)
    c: PointOnObject(g22,g24)
    c: PointOnObject(g23,g24)
    c: Coincident(g24,g-6)
    c: PointOnObject(g23,g1)
    c: DistanceX(g21,g19) = 5.42
    c: Coincident(g25,g26)
    c: Coincident(g26,g27)
    c: Coincident(g27,g28)
    c: Coincident(g28,g29)
    c: Coincident(g29,g30)
    c: Coincident(g30,g25)
    c: Equal(g25, g26-g30) x5
    c: PointOnObject(g25,g31)
    c: PointOnObject(g26,g31)
    c: PointOnObject(g27,g31)
    c: PointOnObject(g28,g31)
    c: PointOnObject(g29,g31)
    c: PointOnObject(g30,g31)
    c: PointOnObject(g30,g0)
    c: DistanceX(g28,g26) = 5.42
    c: Coincident(g31,g-5)
FEATURE [PartDesign::Pocket] Pocket004
  BaseFeature = -> Hole
  Length = 8
  Length2 = 100
  Profile = -> Sketch008
  Type = 0
FEATURE [Sketcher::SketchObject] Sketch009
  MapMode = 5
  Placement = pos=(0,0,7.5) rot=(0,0,1;0rad)
  Support = -> [Pocket004]
  expr: Constraints[51] = Sketch.Constraints[51]
  expr: Constraints[49] = Sketch.Constraints[49]
  expr: Constraints[47] = Sketch.Constraints[47]
  expr: Constraints[40] = Sketch.Constraints[40]
  expr: Constraints[31] = Sketch.Constraints[31]
  expr: Constraints[30] = Sketch.Constraints[30]
  expr: Constraints[29] = Sketch.Constraints[29]
  expr: Constraints[28] = Sketch.Constraints[28]
  expr: Constraints[21] = Sketch.Constraints[21]
  expr: Constraints[20] = Sketch.Constraints[20]
  expr: Constraints[45] = Sketch.Constraints[45]
  expr: Constraints[43] = Sketch.Constraints[43]
  expr: Constraints[42] = Sketch.Constraints[42]
  expr: Constraints[41] = Sketch.Constraints[41]
  expr: Constraints[9] = Sketch.Constraints[9]
  expr: Constraints[8] = Sketch.Constraints[8]
  sketch-geometry (28):
    g0: LineSegment [constr] StartX=-32.5 StartY=15 StartZ=0 EndX=32.5 EndY=15 EndZ=0
    g1: LineSegment [constr] StartX=32.5 StartY=15 StartZ=0 EndX=32.5 EndY=-15 EndZ=0
    g2: LineSegment [constr] StartX=32.5 StartY=-15 StartZ=0 EndX=-32.5 EndY=-15 EndZ=0
    g3: LineSegment [constr] StartX=-32.5 StartY=-15 StartZ=0 EndX=-32.5 EndY=15 EndZ=0
    g4: LineSegment [constr] StartX=-29 StartY=11.5 StartZ=0 EndX=29 EndY=11.5 EndZ=0
    g5: LineSegment [constr] StartX=29 StartY=11.5 StartZ=0 EndX=29 EndY=-11.5 EndZ=0
    g6: LineSegment [constr] StartX=29 StartY=-11.5 StartZ=0 EndX=-29 EndY=-11.5 EndZ=0
    g7: LineSegment [constr] StartX=-29 StartY=-11.5 StartZ=0 EndX=-29 EndY=11.5 EndZ=0
    g8: Circle [constr] CenterX=-29 CenterY=11.5 CenterZ=0 NormalX=0 NormalY=0 NormalZ=1 AngleXU=0 Radius=1.375
    g9: Circle [constr] CenterX=29 CenterY=11.5 CenterZ=0 NormalX=0 NormalY=0 NormalZ=1 AngleXU=0 Radius=1.375
    g10: Circle [constr] CenterX=29 CenterY=-11.5 CenterZ=0 NormalX=0 NormalY=0 NormalZ=1 AngleXU=0 Radius=1.375
    g11: Circle [constr] CenterX=-29 CenterY=-11.5 CenterZ=0 NormalX=0 NormalY=0 NormalZ=1 AngleXU=0 Radius=1.375
    g12: LineSegment [constr] StartX=-29.5 StartY=12 StartZ=0 EndX=29.5 EndY=12 EndZ=0
    g13: LineSegment [constr] StartX=29.5 StartY=12 StartZ=0 EndX=29.5 EndY=-12 EndZ=0
    g14: LineSegment [constr] StartX=29.5 StartY=-12 StartZ=0 EndX=-29.5 EndY=-12 EndZ=0
    g15: LineSegment [constr] StartX=-29.5 StartY=-12 StartZ=0 EndX=-29.5 EndY=12 EndZ=0
    g16: ArcOfCircle [constr] CenterX=-29.5 CenterY=12 CenterZ=0 NormalX=0 NormalY=0 NormalZ=1 AngleXU=0 Radius=3 StartAngle=1.5708 EndAngle=3.14159
    g17: ArcOfCircle [constr] CenterX=29.5 CenterY=12 CenterZ=0 NormalX=0 NormalY=0 NormalZ=1 AngleXU=0 Radius=3 StartAngle=3.7568e-08 EndAngle=1.5708
    g18: ArcOfCircle [constr] CenterX=29.5 CenterY=-12 CenterZ=0 NormalX=0 NormalY=0 NormalZ=1 AngleXU=0 Radius=3 StartAngle=4.71239 EndAngle=6.28319
    g19: ArcOfCircle [constr] CenterX=-29.5 CenterY=-12 CenterZ=0 NormalX=0 NormalY=0 NormalZ=1 AngleXU=0 Radius=3 StartAngle=3.14159 EndAngle=4.71239
    g20: LineSegment [constr] StartX=-29.5 StartY=15 StartZ=0 EndX=29.5 EndY=15 EndZ=0
    g21: LineSegment [constr] StartX=32.5 StartY=12 StartZ=0 EndX=32.5 EndY=-12 EndZ=0
    g22: LineSegment [constr] StartX=29.5 StartY=-15 StartZ=0 EndX=-29.5 EndY=-15 EndZ=0
    g23: LineSegment [constr] StartX=-32.5 StartY=-12 StartZ=0 EndX=-32.5 EndY=12 EndZ=0
    g24: Circle CenterX=-29 CenterY=-11.5 CenterZ=0 NormalX=0 NormalY=0 NormalZ=1 AngleXU=0 Radius=1.07106
    g25: Circle CenterX=29 CenterY=-11.5 CenterZ=0 NormalX=0 NormalY=0 NormalZ=1 AngleXU=0 Radius=1.09378
    g26: Circle CenterX=29 CenterY=11.5 CenterZ=0 NormalX=0 NormalY=0 NormalZ=1 AngleXU=0 Radius=1.14533
    g27: Circle CenterX=-29 CenterY=11.5 CenterZ=0 NormalX=0 NormalY=0 NormalZ=1 AngleXU=0 Radius=1.23522
  constraints (72):
    c: Coincident(g0,g1)
    c: Coincident(g1,g2)
    c: Coincident(g2,g3)
    c: Coincident(g3,g0)
    c: Horizontal(g0)
    c: Horizontal(g2)
    c: Vertical(g1)
    c: Vertical(g3)
    c: DistanceX(g0,g0) = 65
    c: DistanceY(g1,g1) = 30
    c: Symmetric(g0,g0,g-2)
    c: Symmetric(g0,g1,g-1)
    c: Coincident(g4,g5)
    c: Coincident(g5,g6)
    c: Coincident(g6,g7)
    c: Coincident(g7,g4)
    c: Horizontal(g4)
    c: Horizontal(g6)
    c: Vertical(g5)
    c: Vertical(g7)
    c: DistanceX(g4,g4) = 58
    c: DistanceY(g5,g5) = 23
    c: Symmetric(g4,g5,g-1)
    c: Symmetric(g4,g4,g-2)
    c: Coincident(g8,g4)
    c: Coincident(g9,g4)
    c: Coincident(g10,g5)
    c: Coincident(g11,g6)
    c: Radius(g11) = 1.375
    c: Radius(g8) = 1.375
    c: Radius(g9) = 1.375
    c: Radius(g10) = 1.375
    c: Coincident(g12,g13)
    c: Coincident(g13,g14)
    c: Coincident(g14,g15)
    c: Coincident(g15,g12)
    c: Horizontal(g12)
    c: Horizontal(g14)
    c: Vertical(g13)
    c: Vertical(g15)
    c: DistanceX(g4,g12) = 0.5
    c: DistanceY(g4,g12) = 0.5
    c: DistanceY(g13,g5) = 0.5
    c: DistanceX(g14,g6) = 0.5
    c: Coincident(g16,g12)
    c: Radius(g16) = 3
    c: Coincident(g17,g12)
    c: Radius(g17) = 3
    c: Coincident(g18,g13)
    c: Radius(g18) = 3
    c: Coincident(g19,g14)
    c: Radius(g19) = 3
    c: PointOnObject(g16,g0)
    c: PointOnObject(g17,g1)
    c: PointOnObject(g18,g2)
    c: PointOnObject(g19,g3)
    c: Coincident(g20,g16)
    c: Horizontal(g20)
    c: Coincident(g20,g17)
    c: Coincident(g21,g17)
    c: Vertical(g21)
    c: Coincident(g18,g21)
    c: Coincident(g22,g18)
    c: Horizontal(g22)
    c: Coincident(g19,g22)
    c: Coincident(g23,g19)
    c: Vertical(g23)
    c: Coincident(g23,g16)
    c: Coincident(g24,g6)
    c: Coincident(g25,g5)
    c: Coincident(g26,g4)
    c: Coincident(g27,g4)
FEATURE [PartDesign::Hole] Hole001
  BaseFeature = -> Pocket004
  Depth = 25
  DepthType = 1
  Diameter = 2.2
  DrillPoint = 1
  DrillPointAngle = 118
  HoleCutCountersinkAngle = 90
  HoleCutDepth = 0
  HoleCutDiameter = 2
  HoleCutType = 0
  ModelActualThread = false
  Profile = -> Sketch009
  Tapered = false
  TaperedAngle = 90
  ThreadAngle = 60
  ThreadClass = 0
  ThreadCutOffInner = 0.0433013
  ThreadCutOffOuter = 0.0866025
  ThreadDirection = 0
  ThreadFit = 0
  ThreadPitch = 0.4
  ThreadSize = 1
  ThreadType = 1
  Threaded = false
FEATURE [Sketcher::SketchObject] Sketch010
  ExternalGeometry = -> [Hole001]
  MapMode = 5
  Placement = pos=(0,0,0) rot=(1,0,0;3.14159rad)
  Support = -> [Hole001]
  sketch-geometry (32):
    g0: LineSegment [constr] StartX=-29 StartY=20.1024 StartZ=0 EndX=-29 EndY=-21.8008 EndZ=0
    g1: LineSegment [constr] StartX=29 StartY=21.2945 StartZ=0 EndX=29 EndY=-21.3239 EndZ=0
    g2: LineSegment [constr] StartX=-40.5495 StartY=-11.5 StartZ=0 EndX=38.5479 EndY=-11.5 EndZ=0
    g3: LineSegment [constr] StartX=-40.9667 StartY=11.5 StartZ=0 EndX=41.409 EndY=11.5 EndZ=0
    g4: LineSegment StartX=29 StartY=9.13286 StartZ=0 EndX=31.05 EndY=10.3164 EndZ=0
    g5: LineSegment StartX=31.05 StartY=10.3164 StartZ=0 EndX=31.05 EndY=12.6836 EndZ=0
    g6: LineSegment StartX=31.05 StartY=12.6836 StartZ=0 EndX=29 EndY=13.8671 EndZ=0
    g7: LineSegment StartX=29 StartY=13.8671 StartZ=0 EndX=26.95 EndY=12.6836 EndZ=0
    g8: LineSegment StartX=26.95 StartY=12.6836 StartZ=0 EndX=26.95 EndY=10.3164 EndZ=0
    g9: LineSegment StartX=26.95 StartY=10.3164 StartZ=0 EndX=29 EndY=9.13286 EndZ=0
    g10: Circle [constr] CenterX=29 CenterY=11.5 CenterZ=0 NormalX=0 NormalY=0 NormalZ=1 AngleXU=0 Radius=2.36714
    g11: LineSegment StartX=-29 StartY=9.13286 StartZ=0 EndX=-26.95 EndY=10.3164 EndZ=0
    g12: LineSegment StartX=-26.95 StartY=10.3164 StartZ=0 EndX=-26.95 EndY=12.6836 EndZ=0
    g13: LineSegment StartX=-26.95 StartY=12.6836 StartZ=0 EndX=-29 EndY=13.8671 EndZ=0
    g14: LineSegment StartX=-29 StartY=13.8671 StartZ=0 EndX=-31.05 EndY=12.6836 EndZ=0
    g15: LineSegment StartX=-31.05 StartY=12.6836 StartZ=0 EndX=-31.05 EndY=10.3164 EndZ=0
    g16: LineSegment StartX=-31.05 StartY=10.3164 StartZ=0 EndX=-29 EndY=9.13286 EndZ=0
    g17: Circle [constr] CenterX=-29 CenterY=11.5 CenterZ=0 NormalX=0 NormalY=0 NormalZ=1 AngleXU=0 Radius=2.36714
    g18: LineSegment StartX=-29 StartY=-13.8671 StartZ=0 EndX=-26.95 EndY=-12.6836 EndZ=0
    g19: LineSegment StartX=-26.95 StartY=-12.6836 StartZ=0 EndX=-26.95 EndY=-10.3164 EndZ=0
    g20: LineSegment StartX=-26.95 StartY=-10.3164 StartZ=0 EndX=-29 EndY=-9.13286 EndZ=0
    g21: LineSegment StartX=-29 StartY=-9.13286 StartZ=0 EndX=-31.05 EndY=-10.3164 EndZ=0
    g22: LineSegment StartX=-31.05 StartY=-10.3164 StartZ=0 EndX=-31.05 EndY=-12.6836 EndZ=0
    g23: LineSegment StartX=-31.05 StartY=-12.6836 StartZ=0 EndX=-29 EndY=-13.8671 EndZ=0
    g24: Circle [constr] CenterX=-29 CenterY=-11.5 CenterZ=0 NormalX=0 NormalY=0 NormalZ=1 AngleXU=0 Radius=2.36714
    g25: LineSegment StartX=29 StartY=-13.8671 StartZ=0 EndX=31.05 EndY=-12.6836 EndZ=0
    g26: LineSegment StartX=31.05 StartY=-12.6836 StartZ=0 EndX=31.05 EndY=-10.3164 EndZ=0
    g27: LineSegment StartX=31.05 StartY=-10.3164 StartZ=0 EndX=29 EndY=-9.13286 EndZ=0
    g28: LineSegment StartX=29 StartY=-9.13286 StartZ=0 EndX=26.95 EndY=-10.3164 EndZ=0
    g29: LineSegment StartX=26.95 StartY=-10.3164 StartZ=0 EndX=26.95 EndY=-12.6836 EndZ=0
    g30: LineSegment StartX=26.95 StartY=-12.6836 StartZ=0 EndX=29 EndY=-13.8671 EndZ=0
    g31: Circle [constr] CenterX=29 CenterY=-11.5 CenterZ=0 NormalX=0 NormalY=0 NormalZ=1 AngleXU=0 Radius=2.36714
  constraints (72):
    c: Vertical(g0)
    c: Vertical(g1)
    c: Horizontal(g2)
    c: Horizontal(g3)
    c: PointOnObject(g-3,g3)
    c: PointOnObject(g-6,g2)
    c: PointOnObject(g-6,g1)
    c: PointOnObject(g-5,g0)
    c: Coincident(g4,g5)
    c: Coincident(g5,g6)
    c: Coincident(g6,g7)
    c: Coincident(g7,g8)
    c: Coincident(g8,g9)
    c: Coincident(g9,g4)
    c: Equal(g4, g5-g9) x5
    c: PointOnObject(g4,g10)
    c: PointOnObject(g5,g10)
    c: PointOnObject(g6,g10)
    c: PointOnObject(g7,g10)
    c: PointOnObject(g8,g10)
    c: PointOnObject(g9,g10)
    c: Coincident(g10,g-3)
    c: PointOnObject(g9,g1)
    c: DistanceX(g7,g5) = 4.1
    c: Coincident(g11,g12)
    c: Coincident(g12,g13)
    c: Coincident(g13,g14)
    c: Coincident(g14,g15)
    c: Coincident(g15,g16)
    c: Coincident(g16,g11)
    c: Equal(g11, g12-g16) x5
    c: PointOnObject(g11,g17)
    c: PointOnObject(g12,g17)
    c: PointOnObject(g13,g17)
    c: PointOnObject(g14,g17)
    c: PointOnObject(g15,g17)
    c: PointOnObject(g16,g17)
    c: Coincident(g17,g-4)
    c: PointOnObject(g16,g0)
    c: DistanceX(g14,g12) = 4.1
    c: Coincident(g18,g19)
    c: Coincident(g19,g20)
    c: Coincident(g20,g21)
    c: Coincident(g21,g22)
    c: Coincident(g22,g23)
    c: Coincident(g23,g18)
    c: Equal(g18, g19-g23) x5
    c: PointOnObject(g18,g24)
    c: PointOnObject(g19,g24)
    c: PointOnObject(g20,g24)
    c: PointOnObject(g21,g24)
    c: PointOnObject(g22,g24)
    c: PointOnObject(g23,g24)
    c: Coincident(g24,g-5)
    c: PointOnObject(g23,g0)
    c: DistanceX(g21,g19) = 4.1
    c: Coincident(g25,g26)
    c: Coincident(g26,g27)
    c: Coincident(g27,g28)
    c: Coincident(g28,g29)
    c: Coincident(g29,g30)
    c: Coincident(g30,g25)
    c: Equal(g25, g26-g30) x5
    c: PointOnObject(g25,g31)
    c: PointOnObject(g26,g31)
    c: PointOnObject(g27,g31)
    c: PointOnObject(g28,g31)
    c: PointOnObject(g29,g31)
    c: PointOnObject(g30,g31)
    c: Coincident(g31,g-6)
    c: PointOnObject(g30,g1)
    c: DistanceX(g28,g26) = 4.1
FEATURE [PartDesign::Pocket] Pocket005
  BaseFeature = -> Hole001
  Length = 4.5
  Length2 = 100
  Profile = -> Sketch010
  Type = 0
FEATURE [PartDesign::Fillet] Fillet
  Base = -> Pocket005 [Edge312,Edge306,Edge310,Edge308]
  BaseFeature = -> Pocket005
  Radius = 0.6
FEATURE [Sketcher::SketchObject] Sketch011
  ExternalGeometry = -> [Fillet]
  MapMode = 5
  Placement = pos=(32.8,0,0) rot=(0.57735,-0.57735,-0.57735;2.0944rad)
  Support = -> [Fillet]
  sketch-geometry (6):
    g0: LineSegment [constr] StartX=8.50001 StartY=7.5 StartZ=0 EndX=-8.09097 EndY=7.5 EndZ=0
    g1: LineSegment StartX=-9.5 StartY=12 StartZ=0 EndX=9.5 EndY=12 EndZ=0
    g2: LineSegment StartX=9.5 StartY=12 StartZ=0 EndX=9.5 EndY=8.5 EndZ=0
    g3: LineSegment StartX=9.5 StartY=8.5 StartZ=0 EndX=-9.5 EndY=8.5 EndZ=0
    g4: LineSegment StartX=-9.5 StartY=8.5 StartZ=0 EndX=-9.5 EndY=12 EndZ=0
    g5: LineSegment [constr] StartX=0 StartY=15.3767 StartZ=0 EndX=0 EndY=2.68391 EndZ=0
  constraints (16):
    c: Coincident(g0,g-3)
    c: Horizontal(g0)
    c: Coincident(g1,g2)
    c: Coincident(g2,g3)
    c: Coincident(g3,g4)
    c: Coincident(g4,g1)
    c: Horizontal(g1)
    c: Horizontal(g3)
    c: Vertical(g2)
    c: Vertical(g4)
    c: DistanceX(g1,g1) = 19
    c: PointOnObject(g5,g-2)
    c: Vertical(g5)
    c: Symmetric(g1,g1,g5)
    c: PointOnObject(g1,g-4)
    c: DistanceY(g0,g2) = 1
FEATURE [PartDesign::Pocket] Pocket006
  BaseFeature = -> Fillet
  Length = 0.7
  Length2 = 100
  Profile = -> Sketch011
  Type = 0
FEATURE [Sketcher::SketchObject] Sketch012
  ExternalGeometry = -> [Pocket006]
  MapMode = 5
  Placement = pos=(-32.8,0,0) rot=(0.57735,0.57735,0.57735;2.0944rad)
  Support = -> [Pocket006]
  sketch-geometry (15):
    g0: LineSegment [constr] StartX=8.97421 StartY=12 StartZ=0 EndX=8.97421 EndY=4.11024 EndZ=0
    g1: LineSegment [constr] StartX=-5.62579 StartY=12 StartZ=0 EndX=-5.62579 EndY=3.6342 EndZ=0
    g2: LineSegment [constr] StartX=-5.62579 StartY=12 StartZ=0 EndX=8.97421 EndY=12 EndZ=0
    g3: LineSegment [constr] StartX=8.17421 StartY=9.09588 StartZ=0 EndX=8.17421 EndY=3.57816 EndZ=0
    g4: LineSegment [constr] StartX=-4.72579 StartY=9.58242 StartZ=0 EndX=-4.72579 EndY=4.4197 EndZ=0
    g5: LineSegment [constr] StartX=-8.15183 StartY=11.2 StartZ=0 EndX=11.8659 EndY=11.2 EndZ=0
    g6: LineSegment [constr] StartX=-6.90186 StartY=10.9 StartZ=0 EndX=10.8983 EndY=10.9 EndZ=0
    g7: LineSegment StartX=-5.62579 StartY=12 StartZ=0 EndX=-1.62579 EndY=12 EndZ=0
    g8: LineSegment StartX=-1.62579 StartY=12 StartZ=0 EndX=-1.62579 EndY=10.9 EndZ=0
    g9: LineSegment StartX=-1.62579 StartY=10.9 StartZ=0 EndX=-5.62579 EndY=10.9 EndZ=0
    g10: LineSegment StartX=-5.62579 StartY=10.9 StartZ=0 EndX=-5.62579 EndY=12 EndZ=0
    g11: LineSegment StartX=8.97421 StartY=12 StartZ=0 EndX=4.97421 EndY=12 EndZ=0
    g12: LineSegment StartX=4.97421 StartY=12 StartZ=0 EndX=4.97421 EndY=10.9 EndZ=0
    g13: LineSegment StartX=4.97421 StartY=10.9 StartZ=0 EndX=8.97421 EndY=10.9 EndZ=0
    g14: LineSegment StartX=8.97421 StartY=10.9 StartZ=0 EndX=8.97421 EndY=12 EndZ=0
  constraints (38):
    c: Vertical(g0)
    c: DistanceX(g-4,g0) = 1
    c: Vertical(g1)
    c: DistanceX(g1,g-5) = 1
    c: PointOnObject(g2,g-7)
    c: Horizontal(g2)
    c: Vertical(g3)
    c: DistanceX(g3,g0) = 0.8
    c: Vertical(g4)
    c: DistanceX(g1,g4) = 0.9
    c: Horizontal(g5)
    c: DistanceY(g5,g2) = 0.8
    c: Horizontal(g6)
    c: DistanceY(g6,g-7) = 1.1
    c: Coincident(g1,g2)
    c: Coincident(g2,g0)
    c: Coincident(g7,g8)
    c: Coincident(g8,g9)
    c: Coincident(g9,g10)
    c: Coincident(g10,g7)
    c: Horizontal(g7)
    c: Horizontal(g9)
    c: Vertical(g8)
    c: Vertical(g10)
    c: Coincident(g7,g1)
    c: PointOnObject(g8,g6)
    c: Coincident(g11,g12)
    c: Coincident(g12,g13)
    c: Coincident(g13,g14)
    c: Coincident(g14,g11)
    c: Horizontal(g11)
    c: Horizontal(g13)
    c: Vertical(g12)
    c: Vertical(g14)
    c: Coincident(g11,g0)
    c: PointOnObject(g12,g6)
    c: DistanceX(g7,g7) = 4
    c: DistanceX(g11,g11) = 4
FEATURE [PartDesign::Pad] Pad003
  BaseFeature = -> Pocket006
  Length = 4
  Length2 = 100
  Profile = -> Sketch012
  Type = 0
FEATURE [Sketcher::SketchObject] Sketch013
  AttachmentOffset = pos=(0,0,-1.5) rot=(0,0,1;0rad)
  ExternalGeometry = -> [Pad003]
  MapMode = 5
  Placement = pos=(-30.3,0,0) rot=(0.57735,0.57735,0.57735;2.0944rad)
  Support = -> [Pad003]
  sketch-geometry (19):
    g0: LineSegment StartX=8.97421 StartY=10.9 StartZ=0 EndX=4.97421 EndY=10.9 EndZ=0
    g1: LineSegment StartX=4.97421 StartY=10.9 StartZ=0 EndX=4.97421 EndY=10.9 EndZ=0
    g2-g7: Circle [constr] x6 (B-spline internal-alignment scaffolding for g8; pole/knot coordinates omitted)
    g8: BSplineCurve PolesCount=6 KnotsCount=4 Degree=3 IsPeriodic=0
    g9-g12: GeomPoint [constr] x4 (B-spline internal-alignment scaffolding for g8; pole/knot coordinates omitted)
    g13: LineSegment StartX=4.97421 StartY=10.9 StartZ=0 EndX=4.97421 EndY=11.1578 EndZ=0
    g14: LineSegment [constr] StartX=7.97421 StartY=9.43769 StartZ=0 EndX=7.97421 EndY=9.43769 EndZ=0
    g15: LineSegment StartX=-4.62579 StartY=10.3 StartZ=0 EndX=-4.62579 EndY=10.2 EndZ=0
    g16: BSplineCurve PolesCount=6 KnotsCount=4 Degree=3 IsPeriodic=0
    g17: LineSegment StartX=-4.62579 StartY=10.2 StartZ=0 EndX=-1.62579 EndY=10.2 EndZ=0
    g18: LineSegment StartX=-1.62579 StartY=10.2 StartZ=0 EndX=-1.62579 EndY=11.1578 EndZ=0
  constraints (16):
    c: Coincident(g-5,g0)
    c: Coincident(g0,g-5)
    c: Coincident(g0,g1)
    c: Coincident(g1,g-4)
    c: Coincident(g2,g0)
    c: Radius(g2) = 0.02
    c: Equal(g2, g3-g7) x5
    c: PointOnObject(g7,g-4)
    c: InternalAlignment(g2-g7 -> g8) x6
    c: InternalAlignment(g9-g12 -> g8) x4
    c: Coincident(g13,g1)
    c: Coincident(g13,g7)
    c: Vertical(g14)
    c: Symmetric(g-6,g-7,g14)
    c: Coincident(g15,g17)
    c: Coincident(g18,g17)
FEATURE [PartDesign::Fillet] Fillet001
  Base = -> Pad003 [Edge150,Edge180,Edge178,Edge158]
  BaseFeature = -> Pad003
  Radius = 2
FEATURE [PartDesign::Pocket] Pocket007
  BaseFeature = -> Fillet001
  Length = 2.5
  Length2 = 100
  Profile = -> Sketch013
  Type = 0
FEATURE [PartDesign::Fillet] Fillet002
  Base = -> Pocket007 [Edge336,Edge337,Edge261,Edge260]
  BaseFeature = -> Pocket007
  Radius = 1
FEATURE [PartDesign::Fillet] Fillet003
  Base = -> Fillet002 [Edge385,Edge223]
  BaseFeature = -> Fillet002
  Radius = 0.2
FEATURE [PartDesign::Fillet] Fillet004
  Base = -> Fillet003 [Edge230,Edge196,Edge190,Edge109]
  BaseFeature = -> Fillet003
  Radius = 0.1
FEATURE [PartDesign::Body] Body
  Group = -> [Sketch,Sketch001,Pad,Sketch002,Pocket,Sketch003,Pad001,Sketch004,Pad002,Sketch005,Pocket002,Sketch006,Pocket003,Chamfer,Sketch007,Hole,Sketch008,Pocket004,Sketch009,Hole001,Sketch010,Pocket005,Fillet,Sketch011,Pocket006,Sketch012,Pad003,Fillet001,Sketch013,Pocket007,Fillet002,Fillet003,Fillet004]
  Origin = -> Origin
  Tip = -> Fillet004
FEATURE [Mesh::Feature] Mesh  label="Fillet004 (Meshed)"
